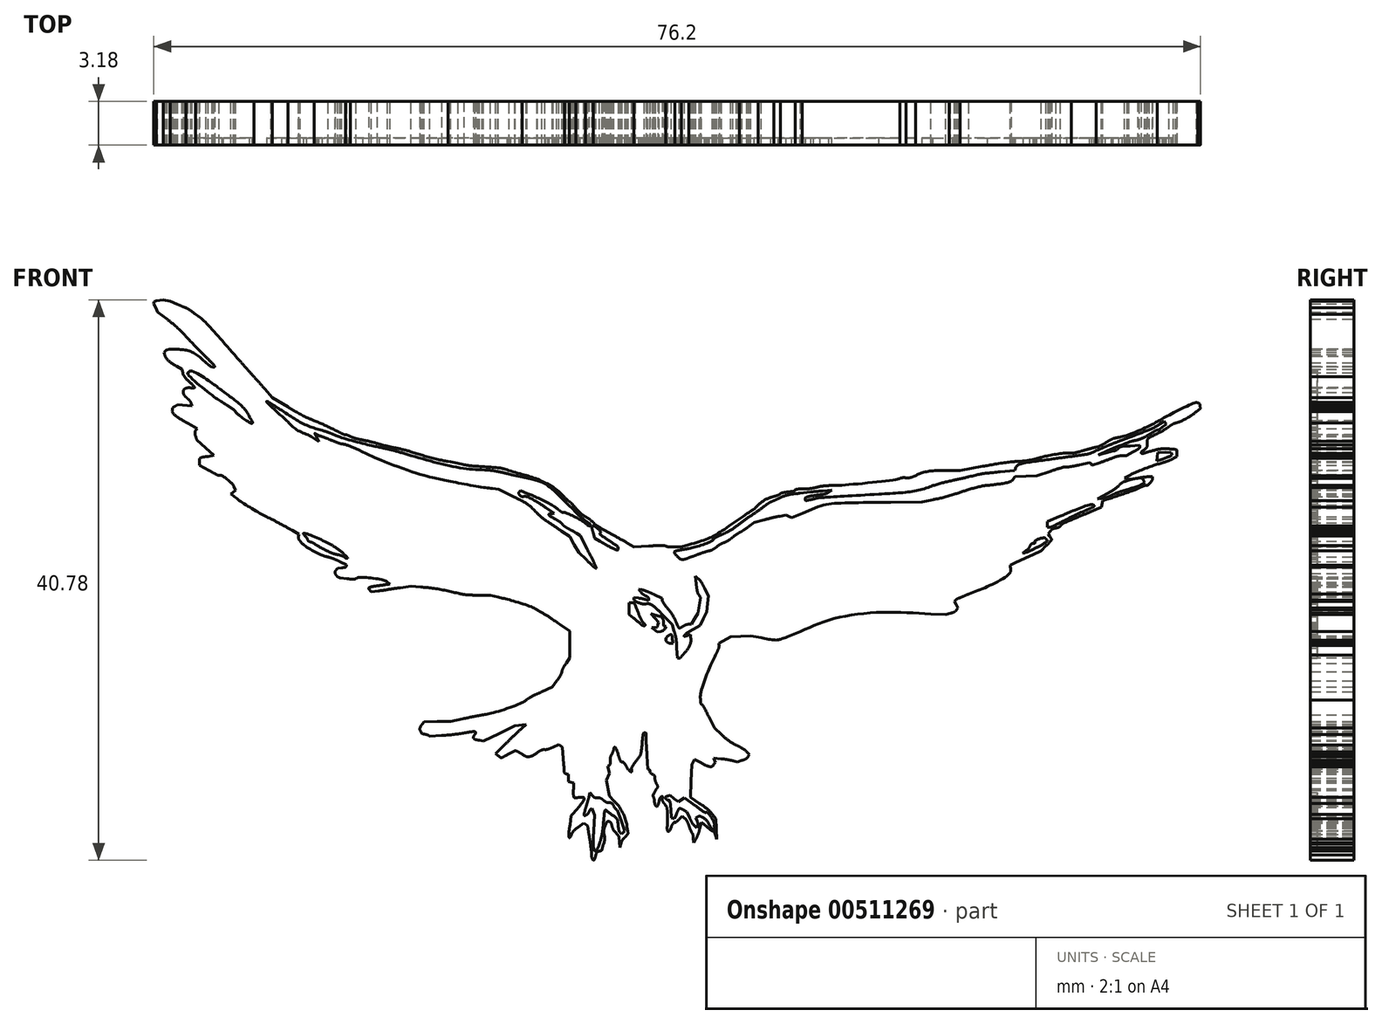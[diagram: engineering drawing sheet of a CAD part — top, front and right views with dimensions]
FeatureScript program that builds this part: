
annotation { "Feature Type Name" : "Feature", "Feature Type Description" : "" }
export const myFeature = defineFeature(function(context is Context, id is Id, definition is map)
    precondition{}
    {
        {
            var Q0;
            Q0=qCreatedBy(makeId("Front.planeOp"),FACE);
            var sketch = newSketch(context, id + "F0", { "sketchPlane" : qUnion([Q0])});
            skFitSpline(sketch, "E0", {"points": [v(-6.24, -23.55) * mm, v(-6.28, -23.27) * mm, v(-6.35, -22.74) * mm, v(-6.4, -22.37) * mm]});
            skFitSpline(sketch, "E1", {"points": [v(-6.51, -21.7) * mm, v(-6.6, -21.64) * mm, v(-6.7, -21.58) * mm, v(-6.8, -21.52) * mm]});
            skLineSegment(sketch, "E2", {"start": v(-6.4, -22.37) * mm, "end": v(-6.51, -21.7) * mm});
            skFitSpline(sketch, "E3", {"points": [v(-7.17, -21.78) * mm, v(-7.37, -21.93) * mm, v(-7.58, -22.14) * mm, v(-7.65, -22.25) * mm]});
            skFitSpline(sketch, "E4", {"points": [v(-7.65, -22.25) * mm, v(-7.83, -22.59) * mm, v(-7.89, -22.36) * mm, v(-7.8, -21.65) * mm]});
            skLineSegment(sketch, "E5", {"start": v(-6.8, -21.52) * mm, "end": v(-7.17, -21.78) * mm});
            skFitSpline(sketch, "E6", {"points": [v(-7.72, -20.99) * mm, v(-7.42, -20.64) * mm, v(-6.77, -19.7) * mm, v(-7.27, -19.67) * mm]});
            skFitSpline(sketch, "E7", {"points": [v(-7.27, -19.67) * mm, v(-7.47, -19.67) * mm, v(-7.54, -19.5) * mm, v(-7.54, -19) * mm]});
            skLineSegment(sketch, "E8", {"start": v(-7.8, -21.65) * mm, "end": v(-7.72, -20.99) * mm});
            skFitSpline(sketch, "E9", {"points": [v(-7.54, -18.6) * mm, v(-7.66, -18.56) * mm, v(-7.78, -18.52) * mm, v(-7.9, -18.49) * mm]});
            skFitSpline(sketch, "E10", {"points": [v(-7.9, -18.49) * mm, v(-7.9, -18.31) * mm, v(-7.9, -18.14) * mm, v(-7.9, -17.97) * mm]});
            skFitSpline(sketch, "E11", {"points": [v(-7.9, -17.97) * mm, v(-8.05, -17.94) * mm, v(-8.18, -17.87) * mm, v(-8.23, -17.75) * mm]});
            skFitSpline(sketch, "E12", {"points": [v(-8.23, -17.75) * mm, v(-8.23, -17.7) * mm, v(-8.25, -17.27) * mm, v(-8.3, -16.82) * mm]});
            skLineSegment(sketch, "E13", {"start": v(-7.54, -19) * mm, "end": v(-7.54, -18.6) * mm});
            skFitSpline(sketch, "E14", {"points": [v(-8.37, -16) * mm, v(-8.44, -15.93) * mm, v(-8.52, -15.86) * mm, v(-8.6, -15.8) * mm]});
            skLineSegment(sketch, "E15", {"start": v(-8.3, -16.82) * mm, "end": v(-8.37, -16) * mm});
            skFitSpline(sketch, "E16", {"points": [v(-9.02, -15.98) * mm, v(-9.26, -16.08) * mm, v(-9.53, -16.16) * mm, v(-9.64, -16.16) * mm]});
            skFitSpline(sketch, "E17", {"points": [v(-9.64, -16.16) * mm, v(-9.75, -16.16) * mm, v(-10, -16.26) * mm, v(-10.2, -16.38) * mm]});
            skFitSpline(sketch, "E18", {"points": [v(-10.2, -16.38) * mm, v(-10.6, -16.64) * mm, v(-10.99, -16.67) * mm, v(-11.32, -16.48) * mm]});
            skFitSpline(sketch, "E19", {"points": [v(-11.32, -16.48) * mm, v(-11.47, -16.4) * mm, v(-11.62, -16.3) * mm, v(-11.77, -16.23) * mm]});
            skLineSegment(sketch, "E20", {"start": v(-8.6, -15.8) * mm, "end": v(-9.02, -15.98) * mm});
            skFitSpline(sketch, "E21", {"points": [v(-12.23, -16.47) * mm, v(-12.75, -16.74) * mm, v(-12.84, -16.75) * mm, v(-13.06, -16.58) * mm]});
            skLineSegment(sketch, "E22", {"start": v(-11.77, -16.23) * mm, "end": v(-12.23, -16.47) * mm});
            skFitSpline(sketch, "E23", {"points": [v(-12.45, -15.7) * mm, v(-12.02, -15.29) * mm, v(-11.52, -14.82) * mm, v(-11.34, -14.65) * mm]});
            skLineSegment(sketch, "E24", {"start": v(-13.06, -16.58) * mm, "end": v(-13.23, -16.46) * mm});
            skLineSegment(sketch, "E25", {"start": v(-13.23, -16.46) * mm, "end": v(-12.45, -15.7) * mm});
            skFitSpline(sketch, "E26", {"points": [v(-11, -14.35) * mm, v(-11.27, -14.38) * mm, v(-11.54, -14.4) * mm, v(-11.81, -14.43) * mm]});
            skLineSegment(sketch, "E27", {"start": v(-11.34, -14.65) * mm, "end": v(-11, -14.35) * mm});
            skFitSpline(sketch, "E28", {"points": [v(-14.4, -15.48) * mm, v(-14.74, -15.4) * mm, v(-14.84, -15.29) * mm, v(-14.72, -15.07) * mm]});
            skFitSpline(sketch, "E29", {"points": [v(-14.72, -15.07) * mm, v(-14.68, -14.99) * mm, v(-14.67, -14.9) * mm, v(-14.7, -14.87) * mm]});
            skFitSpline(sketch, "E30", {"points": [v(-14.7, -14.87) * mm, v(-14.75, -14.85) * mm, v(-15.12, -14.89) * mm, v(-15.54, -14.96) * mm]});
            skFitSpline(sketch, "E31", {"points": [v(-15.54, -14.96) * mm, v(-15.96, -15.03) * mm, v(-16.69, -15.1) * mm, v(-17.16, -15.13) * mm]});
            skLineSegment(sketch, "E32", {"start": v(-11.81, -14.43) * mm, "end": v(-12.96, -14.99) * mm});
            skLineSegment(sketch, "E33", {"start": v(-12.96, -14.99) * mm, "end": v(-14.1, -15.55) * mm});
            skLineSegment(sketch, "E34", {"start": v(-14.1, -15.55) * mm, "end": v(-14.4, -15.48) * mm});
            skFitSpline(sketch, "E35", {"points": [v(-18, -15.19) * mm, v(-18.22, -15.08) * mm, v(-18.58, -14.98) * mm, v(-18.64, -14.86) * mm]});
            skFitSpline(sketch, "E36", {"points": [v(-18.64, -14.86) * mm, v(-18.73, -14.71) * mm, v(-18.66, -14.47) * mm, v(-18.56, -14.32) * mm]});
            skLineSegment(sketch, "E37", {"start": v(-17.16, -15.13) * mm, "end": v(-18, -15.19) * mm});
            skFitSpline(sketch, "E38", {"points": [v(-15.58, -13.92) * mm, v(-15.09, -13.82) * mm, v(-14.46, -13.7) * mm, v(-14.2, -13.64) * mm]});
            skFitSpline(sketch, "E39", {"points": [v(-14.2, -13.64) * mm, v(-13.41, -13.49) * mm, v(-11.3, -12.76) * mm, v(-10.94, -12.52) * mm]});
            skFitSpline(sketch, "E40", {"points": [v(-10.94, -12.52) * mm, v(-10.75, -12.4) * mm, v(-10.26, -12.14) * mm, v(-9.85, -11.95) * mm]});
            skLineSegment(sketch, "E41", {"start": v(-18.56, -14.32) * mm, "end": v(-18.43, -14.14) * mm});
            skLineSegment(sketch, "E42", {"start": v(-18.43, -14.14) * mm, "end": v(-17.46, -14.13) * mm});
            skLineSegment(sketch, "E43", {"start": v(-17.46, -14.13) * mm, "end": v(-16.48, -14.1) * mm});
            skLineSegment(sketch, "E44", {"start": v(-16.48, -14.1) * mm, "end": v(-15.58, -13.92) * mm});
            skFitSpline(sketch, "E45", {"points": [v(-8.77, -11.16) * mm, v(-8.6, -10.92) * mm, v(-8.43, -10.63) * mm, v(-8.4, -10.5) * mm]});
            skFitSpline(sketch, "E46", {"points": [v(-8.4, -10.5) * mm, v(-8.36, -10.38) * mm, v(-8.22, -10.1) * mm, v(-8.07, -9.88) * mm]});
            skLineSegment(sketch, "E47", {"start": v(-9.85, -11.95) * mm, "end": v(-9.09, -11.6) * mm});
            skLineSegment(sketch, "E48", {"start": v(-9.09, -11.6) * mm, "end": v(-8.77, -11.16) * mm});
            skFitSpline(sketch, "E49", {"points": [v(-8.52, -7.07) * mm, v(-9.26, -6.55) * mm, v(-9.66, -6.3) * mm, v(-10.16, -6.02) * mm]});
            skFitSpline(sketch, "E50", {"points": [v(-10.16, -6.02) * mm, v(-10.52, -5.82) * mm, v(-12.11, -5.3) * mm, v(-13.02, -5.08) * mm]});
            skLineSegment(sketch, "E51", {"start": v(-8.07, -9.88) * mm, "end": v(-7.8, -9.48) * mm});
            skLineSegment(sketch, "E52", {"start": v(-7.8, -9.48) * mm, "end": v(-7.82, -8.51) * mm});
            skLineSegment(sketch, "E53", {"start": v(-7.82, -8.51) * mm, "end": v(-7.83, -7.55) * mm});
            skLineSegment(sketch, "E54", {"start": v(-7.83, -7.55) * mm, "end": v(-8.52, -7.07) * mm});
            skFitSpline(sketch, "E55", {"points": [v(-14.5, -4.93) * mm, v(-15, -4.92) * mm, v(-15.65, -4.86) * mm, v(-15.94, -4.8) * mm]});
            skFitSpline(sketch, "E56", {"points": [v(-15.94, -4.8) * mm, v(-16.93, -4.57) * mm, v(-17.95, -4.4) * mm, v(-18.66, -4.34) * mm]});
            skLineSegment(sketch, "E57", {"start": v(-13.02, -5.08) * mm, "end": v(-13.6, -4.94) * mm});
            skLineSegment(sketch, "E58", {"start": v(-13.6, -4.94) * mm, "end": v(-14.5, -4.93) * mm});
            skFitSpline(sketch, "E59", {"points": [v(-20.12, -4.38) * mm, v(-20.54, -4.44) * mm, v(-20.97, -4.5) * mm, v(-21.07, -4.52) * mm]});
            skFitSpline(sketch, "E60", {"points": [v(-21.07, -4.52) * mm, v(-21.17, -4.54) * mm, v(-21.48, -4.58) * mm, v(-21.75, -4.62) * mm]});
            skLineSegment(sketch, "E61", {"start": v(-18.66, -4.34) * mm, "end": v(-19.36, -4.28) * mm});
            skLineSegment(sketch, "E62", {"start": v(-19.36, -4.28) * mm, "end": v(-20.12, -4.38) * mm});
            skFitSpline(sketch, "E63", {"points": [v(-22.25, -4.68) * mm, v(-22.44, -4.4) * mm, v(-21.99, -4.27) * mm, v(-21.86, -4.25) * mm]});
            skFitSpline(sketch, "E64", {"points": [v(-21.86, -4.25) * mm, v(-21.54, -4.2) * mm, v(-21.23, -4.16) * mm, v(-20.9, -4.11) * mm]});
            skLineSegment(sketch, "E65", {"start": v(-21.75, -4.62) * mm, "end": v(-22.25, -4.68) * mm});
            skFitSpline(sketch, "E66", {"points": [v(-21.07, -4) * mm, v(-21.28, -3.86) * mm, v(-23.16, -3.64) * mm, v(-23.38, -3.73) * mm]});
            skFitSpline(sketch, "E67", {"points": [v(-23.38, -3.73) * mm, v(-23.47, -3.76) * mm, v(-23.76, -3.76) * mm, v(-24.03, -3.72) * mm]});
            skLineSegment(sketch, "E68", {"start": v(-20.9, -4.11) * mm, "end": v(-21.07, -4) * mm});
            skFitSpline(sketch, "E69", {"points": [v(-24.52, -3.66) * mm, v(-24.7, -3.6) * mm, v(-24.8, -3.5) * mm, v(-24.89, -3.36) * mm]});
            skFitSpline(sketch, "E70", {"points": [v(-24.89, -3.36) * mm, v(-24.89, -3.2) * mm, v(-24.8, -3.05) * mm, v(-24.7, -2.97) * mm]});
            skLineSegment(sketch, "E71", {"start": v(-24.03, -3.72) * mm, "end": v(-24.52, -3.66) * mm});
            skFitSpline(sketch, "E72", {"points": [v(-24.42, -2.94) * mm, v(-24.23, -2.9) * mm, v(-24.12, -2.88) * mm, v(-24.07, -2.71) * mm]});
            skLineSegment(sketch, "E73", {"start": v(-24.7, -2.97) * mm, "end": v(-24.42, -2.94) * mm});
            skFitSpline(sketch, "E74", {"points": [v(-24.54, -2.5) * mm, v(-24.8, -2.37) * mm, v(-25.2, -2.22) * mm, v(-25.42, -2.15) * mm]});
            skFitSpline(sketch, "E75", {"points": [v(-25.42, -2.15) * mm, v(-25.9, -2) * mm, v(-27.2, -1.26) * mm, v(-27.43, -1) * mm]});
            skFitSpline(sketch, "E76", {"points": [v(-27.43, -1) * mm, v(-27.52, -0.9) * mm, v(-27.58, -0.74) * mm, v(-27.56, -0.65) * mm]});
            skLineSegment(sketch, "E77", {"start": v(-24.07, -2.71) * mm, "end": v(-24.54, -2.5) * mm});
            skFitSpline(sketch, "E78", {"points": [v(-28.02, -0.2) * mm, v(-28.3, -0.05) * mm, v(-28.98, 0.32) * mm, v(-29.55, 0.61) * mm]});
            skFitSpline(sketch, "E79", {"points": [v(-29.55, 0.61) * mm, v(-30.46, 1.08) * mm, v(-31.74, 1.87) * mm, v(-32.3, 2.3) * mm]});
            skLineSegment(sketch, "E80", {"start": v(-27.56, -0.65) * mm, "end": v(-27.52, -0.49) * mm});
            skLineSegment(sketch, "E81", {"start": v(-27.52, -0.49) * mm, "end": v(-28.02, -0.2) * mm});
            skFitSpline(sketch, "E82", {"points": [v(-32.47, 2.43) * mm, v(-32.36, 2.52) * mm, v(-32.24, 2.6) * mm, v(-32.13, 2.7) * mm]});
            skLineSegment(sketch, "E83", {"start": v(-32.3, 2.3) * mm, "end": v(-32.47, 2.43) * mm});
            skFitSpline(sketch, "E84", {"points": [v(-32.25, 2.94) * mm, v(-32.37, 3.15) * mm, v(-33.18, 3.78) * mm, v(-33.35, 3.78) * mm]});
            skFitSpline(sketch, "E85", {"points": [v(-33.35, 3.78) * mm, v(-33.38, 3.78) * mm, v(-33.72, 3.95) * mm, v(-34.09, 4.16) * mm]});
            skLineSegment(sketch, "E86", {"start": v(-32.13, 2.7) * mm, "end": v(-32.25, 2.94) * mm});
            skFitSpline(sketch, "E87", {"points": [v(-34.76, 4.73) * mm, v(-34.76, 5) * mm, v(-34.62, 5.1) * mm, v(-34.14, 5.17) * mm]});
            skLineSegment(sketch, "E88", {"start": v(-34.09, 4.16) * mm, "end": v(-34.76, 4.53) * mm});
            skLineSegment(sketch, "E89", {"start": v(-34.76, 4.53) * mm, "end": v(-34.76, 4.73) * mm});
            skFitSpline(sketch, "E90", {"points": [v(-34.95, 6.37) * mm, v(-35.07, 6.68) * mm, v(-35.09, 7) * mm, v(-34.93, 7.18) * mm]});
            skLineSegment(sketch, "E91", {"start": v(-34.14, 5.17) * mm, "end": v(-33.74, 5.24) * mm});
            skLineSegment(sketch, "E92", {"start": v(-33.74, 5.24) * mm, "end": v(-34.34, 5.8) * mm});
            skLineSegment(sketch, "E93", {"start": v(-34.34, 5.8) * mm, "end": v(-34.95, 6.37) * mm});
            skFitSpline(sketch, "E94", {"points": [v(-35.59, 7.56) * mm, v(-36.27, 7.96) * mm, v(-36.74, 8.38) * mm, v(-36.74, 8.6) * mm]});
            skFitSpline(sketch, "E95", {"points": [v(-36.74, 8.6) * mm, v(-36.74, 8.66) * mm, v(-36.65, 8.76) * mm, v(-36.54, 8.82) * mm]});
            skLineSegment(sketch, "E96", {"start": v(-34.93, 7.18) * mm, "end": v(-35.59, 7.56) * mm});
            skFitSpline(sketch, "E97", {"points": [v(-35.37, 9) * mm, v(-35.39, 9.08) * mm, v(-35.53, 9.26) * mm, v(-35.67, 9.4) * mm]});
            skFitSpline(sketch, "E98", {"points": [v(-35.67, 9.4) * mm, v(-35.81, 9.54) * mm, v(-35.93, 9.72) * mm, v(-35.93, 9.81) * mm]});
            skFitSpline(sketch, "E99", {"points": [v(-35.93, 9.81) * mm, v(-35.93, 10) * mm, v(-35.68, 10.16) * mm, v(-35.4, 10.16) * mm]});
            skFitSpline(sketch, "E100", {"points": [v(-35.4, 10.16) * mm, v(-35.13, 10.16) * mm, v(-35.17, 10.26) * mm, v(-35.57, 10.65) * mm]});
            skFitSpline(sketch, "E101", {"points": [v(-35.57, 10.65) * mm, v(-35.76, 10.84) * mm, v(-35.95, 11.11) * mm, v(-35.98, 11.25) * mm]});
            skLineSegment(sketch, "E102", {"start": v(-36.54, 8.82) * mm, "end": v(-36.35, 8.92) * mm});
            skLineSegment(sketch, "E103", {"start": v(-36.35, 8.92) * mm, "end": v(-35.84, 8.88) * mm});
            skLineSegment(sketch, "E104", {"start": v(-35.84, 8.88) * mm, "end": v(-35.32, 8.83) * mm});
            skLineSegment(sketch, "E105", {"start": v(-35.32, 8.83) * mm, "end": v(-35.37, 9) * mm});
            skFitSpline(sketch, "E106", {"points": [v(-36.41, 11.73) * mm, v(-36.81, 11.96) * mm, v(-37.22, 12.36) * mm, v(-37.3, 12.59) * mm]});
            skLineSegment(sketch, "E107", {"start": v(-35.98, 11.25) * mm, "end": v(-36.03, 11.5) * mm});
            skLineSegment(sketch, "E108", {"start": v(-36.03, 11.5) * mm, "end": v(-36.41, 11.73) * mm});
            skFitSpline(sketch, "E109", {"points": [v(-36.6, 12.95) * mm, v(-35.78, 12.9) * mm, v(-35.02, 12.6) * mm, v(-34.3, 12) * mm]});
            skFitSpline(sketch, "E110", {"points": [v(-34.3, 12) * mm, v(-34.1, 11.82) * mm, v(-33.9, 11.69) * mm, v(-33.86, 11.69) * mm]});
            skFitSpline(sketch, "E111", {"points": [v(-33.86, 11.69) * mm, v(-33.66, 11.69) * mm, v(-33.81, 11.91) * mm, v(-34.34, 12.44) * mm]});
            skFitSpline(sketch, "E112", {"points": [v(-34.34, 12.44) * mm, v(-34.64, 12.74) * mm, v(-35.25, 13.36) * mm, v(-35.67, 13.8) * mm]});
            skFitSpline(sketch, "E113", {"points": [v(-35.67, 13.8) * mm, v(-36.1, 14.26) * mm, v(-36.76, 14.86) * mm, v(-37.13, 15.15) * mm]});
            skLineSegment(sketch, "E114", {"start": v(-37.3, 12.59) * mm, "end": v(-37.35, 12.73) * mm});
            skLineSegment(sketch, "E115", {"start": v(-37.35, 12.73) * mm, "end": v(-37.19, 12.9) * mm});
            skLineSegment(sketch, "E116", {"start": v(-37.19, 12.9) * mm, "end": v(-36.96, 12.97) * mm});
            skLineSegment(sketch, "E117", {"start": v(-36.96, 12.97) * mm, "end": v(-36.6, 12.95) * mm});
            skFitSpline(sketch, "E118", {"points": [v(-36.39, 16.24) * mm, v(-36.11, 16.12) * mm, v(-35.83, 16) * mm, v(-35.75, 15.97) * mm]});
            skFitSpline(sketch, "E119", {"points": [v(-35.75, 15.97) * mm, v(-35.68, 15.95) * mm, v(-35.36, 15.74) * mm, v(-35.06, 15.5) * mm]});
            skFitSpline(sketch, "E120", {"points": [v(-35.06, 15.5) * mm, v(-34.53, 15.1) * mm, v(-33.65, 14.19) * mm, v(-31.84, 12.14) * mm]});
            skFitSpline(sketch, "E121", {"points": [v(-31.84, 12.14) * mm, v(-31.4, 11.63) * mm, v(-30.93, 11.1) * mm, v(-30.81, 10.97) * mm]});
            skFitSpline(sketch, "E122", {"points": [v(-30.81, 10.97) * mm, v(-30.69, 10.84) * mm, v(-30.33, 10.44) * mm, v(-30.02, 10.09) * mm]});
            skLineSegment(sketch, "E123", {"start": v(-37.13, 15.15) * mm, "end": v(-37.81, 15.67) * mm});
            skLineSegment(sketch, "E124", {"start": v(-37.81, 15.67) * mm, "end": v(-37.96, 15.98) * mm});
            skLineSegment(sketch, "E125", {"start": v(-37.96, 15.98) * mm, "end": v(-38.1, 16.28) * mm});
            skLineSegment(sketch, "E126", {"start": v(-38.1, 16.28) * mm, "end": v(-38.07, 16.42) * mm});
            skLineSegment(sketch, "E127", {"start": v(-38.07, 16.42) * mm, "end": v(-37.92, 16.5) * mm});
            skLineSegment(sketch, "E128", {"start": v(-37.92, 16.5) * mm, "end": v(-37.42, 16.57) * mm});
            skLineSegment(sketch, "E129", {"start": v(-37.42, 16.57) * mm, "end": v(-36.89, 16.46) * mm});
            skLineSegment(sketch, "E130", {"start": v(-36.89, 16.46) * mm, "end": v(-36.39, 16.24) * mm});
            skFitSpline(sketch, "E131", {"points": [v(-28.33, 8.77) * mm, v(-27.72, 8.4) * mm, v(-26.86, 7.95) * mm, v(-26.43, 7.77) * mm]});
            skFitSpline(sketch, "E132", {"points": [v(-26.43, 7.77) * mm, v(-26, 7.6) * mm, v(-25.33, 7.3) * mm, v(-24.94, 7.1) * mm]});
            skFitSpline(sketch, "E133", {"points": [v(-24.94, 7.1) * mm, v(-24.54, 6.9) * mm, v(-24.18, 6.74) * mm, v(-24.14, 6.74) * mm]});
            skFitSpline(sketch, "E134", {"points": [v(-24.14, 6.74) * mm, v(-24.1, 6.74) * mm, v(-23.93, 6.69) * mm, v(-23.77, 6.62) * mm]});
            skFitSpline(sketch, "E135", {"points": [v(-23.77, 6.62) * mm, v(-23.62, 6.55) * mm, v(-23.2, 6.43) * mm, v(-22.86, 6.36) * mm]});
            skFitSpline(sketch, "E136", {"points": [v(-22.86, 6.36) * mm, v(-22.51, 6.29) * mm, v(-22, 6.16) * mm, v(-21.74, 6.08) * mm]});
            skFitSpline(sketch, "E137", {"points": [v(-21.74, 6.08) * mm, v(-21.47, 6) * mm, v(-20.94, 5.88) * mm, v(-20.57, 5.8) * mm]});
            skFitSpline(sketch, "E138", {"points": [v(-20.57, 5.8) * mm, v(-20.2, 5.72) * mm, v(-19.63, 5.58) * mm, v(-19.31, 5.48) * mm]});
            skFitSpline(sketch, "E139", {"points": [v(-19.31, 5.48) * mm, v(-18.41, 5.21) * mm, v(-17.35, 4.94) * mm, v(-16.66, 4.8) * mm]});
            skFitSpline(sketch, "E140", {"points": [v(-16.66, 4.8) * mm, v(-15.32, 4.53) * mm, v(-15.1, 4.5) * mm, v(-14.04, 4.41) * mm]});
            skFitSpline(sketch, "E141", {"points": [v(-14.04, 4.41) * mm, v(-12.89, 4.33) * mm, v(-12.7, 4.29) * mm, v(-11.27, 3.85) * mm]});
            skFitSpline(sketch, "E142", {"points": [v(-11.27, 3.85) * mm, v(-10.21, 3.53) * mm, v(-8.79, 2.76) * mm, v(-8.2, 2.2) * mm]});
            skFitSpline(sketch, "E143", {"points": [v(-8.2, 2.2) * mm, v(-8.1, 2.1) * mm, v(-7.94, 1.97) * mm, v(-7.85, 1.89) * mm]});
            skFitSpline(sketch, "E144", {"points": [v(-7.85, 1.89) * mm, v(-7.76, 1.81) * mm, v(-7.54, 1.59) * mm, v(-7.36, 1.39) * mm]});
            skFitSpline(sketch, "E145", {"points": [v(-7.36, 1.39) * mm, v(-7.2, 1.19) * mm, v(-6.88, 0.92) * mm, v(-6.68, 0.79) * mm]});
            skFitSpline(sketch, "E146", {"points": [v(-6.68, 0.79) * mm, v(-6.47, 0.66) * mm, v(-6.2, 0.46) * mm, v(-6.1, 0.34) * mm]});
            skFitSpline(sketch, "E147", {"points": [v(-6.1, 0.34) * mm, v(-5.97, 0.23) * mm, v(-5.46, -0.1) * mm, v(-4.94, -0.4) * mm]});
            skFitSpline(sketch, "E148", {"points": [v(-4.94, -0.4) * mm, v(-4.42, -0.68) * mm, v(-3.8, -1.03) * mm, v(-3.58, -1.16) * mm]});
            skLineSegment(sketch, "E149", {"start": v(-30.02, 10.09) * mm, "end": v(-29.46, 9.45) * mm});
            skLineSegment(sketch, "E150", {"start": v(-29.46, 9.45) * mm, "end": v(-28.33, 8.77) * mm});
            skFitSpline(sketch, "E151", {"points": [v(-2.07, -1.35) * mm, v(-1.47, -1.32) * mm, v(-0.91, -1.32) * mm, v(-0.83, -1.36) * mm]});
            skFitSpline(sketch, "E152", {"points": [v(-0.83, -1.36) * mm, v(-0.74, -1.39) * mm, v(-0.45, -1.42) * mm, v(-0.18, -1.42) * mm]});
            skLineSegment(sketch, "E153", {"start": v(-3.58, -1.16) * mm, "end": v(-3.16, -1.41) * mm});
            skLineSegment(sketch, "E154", {"start": v(-3.16, -1.41) * mm, "end": v(-2.07, -1.35) * mm});
            skFitSpline(sketch, "E155", {"points": [v(0.85, -1.26) * mm, v(2.23, -0.82) * mm, v(2.98, -0.44) * mm, v(4.53, 0.61) * mm]});
            skFitSpline(sketch, "E156", {"points": [v(4.53, 0.61) * mm, v(5.51, 1.29) * mm, v(5.64, 1.38) * mm, v(5.91, 1.63) * mm]});
            skFitSpline(sketch, "E157", {"points": [v(5.91, 1.63) * mm, v(6.15, 1.85) * mm, v(6.66, 2.13) * mm, v(7.05, 2.25) * mm]});
            skFitSpline(sketch, "E158", {"points": [v(7.05, 2.25) * mm, v(7.25, 2.32) * mm, v(7.46, 2.4) * mm, v(7.52, 2.45) * mm]});
            skFitSpline(sketch, "E159", {"points": [v(7.52, 2.45) * mm, v(7.57, 2.5) * mm, v(7.83, 2.55) * mm, v(8.08, 2.58) * mm]});
            skFitSpline(sketch, "E160", {"points": [v(8.08, 2.58) * mm, v(8.33, 2.61) * mm, v(8.56, 2.67) * mm, v(8.59, 2.71) * mm]});
            skFitSpline(sketch, "E161", {"points": [v(8.59, 2.71) * mm, v(8.61, 2.76) * mm, v(8.85, 2.8) * mm, v(9.1, 2.8) * mm]});
            skFitSpline(sketch, "E162", {"points": [v(9.1, 2.8) * mm, v(9.36, 2.8) * mm, v(9.81, 2.85) * mm, v(10.1, 2.91) * mm]});
            skFitSpline(sketch, "E163", {"points": [v(10.1, 2.91) * mm, v(10.4, 2.98) * mm, v(10.9, 3.04) * mm, v(11.23, 3.05) * mm]});
            skFitSpline(sketch, "E164", {"points": [v(11.23, 3.05) * mm, v(11.98, 3.08) * mm, v(15.98, 3.5) * mm, v(16.22, 3.57) * mm]});
            skFitSpline(sketch, "E165", {"points": [v(16.22, 3.57) * mm, v(16.31, 3.6) * mm, v(16.52, 3.62) * mm, v(16.67, 3.61) * mm]});
            skFitSpline(sketch, "E166", {"points": [v(16.67, 3.61) * mm, v(16.82, 3.6) * mm, v(17.12, 3.67) * mm, v(17.35, 3.77) * mm]});
            skFitSpline(sketch, "E167", {"points": [v(17.35, 3.77) * mm, v(17.88, 4) * mm, v(18.84, 4.14) * mm, v(19.81, 4.14) * mm]});
            skLineSegment(sketch, "E168", {"start": v(-0.18, -1.42) * mm, "end": v(0.32, -1.43) * mm});
            skLineSegment(sketch, "E169", {"start": v(0.32, -1.43) * mm, "end": v(0.85, -1.26) * mm});
            skFitSpline(sketch, "E170", {"points": [v(22.26, 4.44) * mm, v(23.19, 4.61) * mm, v(24.3, 4.77) * mm, v(24.75, 4.8) * mm]});
            skFitSpline(sketch, "E171", {"points": [v(24.75, 4.8) * mm, v(25.2, 4.83) * mm, v(25.88, 4.94) * mm, v(26.27, 5.04) * mm]});
            skFitSpline(sketch, "E172", {"points": [v(26.27, 5.04) * mm, v(26.94, 5.2) * mm, v(28.3, 5.42) * mm, v(28.7, 5.4) * mm]});
            skFitSpline(sketch, "E173", {"points": [v(28.7, 5.4) * mm, v(28.8, 5.4) * mm, v(29.18, 5.49) * mm, v(29.55, 5.59) * mm]});
            skFitSpline(sketch, "E174", {"points": [v(29.55, 5.59) * mm, v(29.93, 5.69) * mm, v(30.35, 5.8) * mm, v(30.5, 5.84) * mm]});
            skFitSpline(sketch, "E175", {"points": [v(30.5, 5.84) * mm, v(30.65, 5.88) * mm, v(30.97, 6.03) * mm, v(31.22, 6.18) * mm]});
            skFitSpline(sketch, "E176", {"points": [v(31.22, 6.18) * mm, v(31.46, 6.33) * mm, v(31.79, 6.48) * mm, v(31.94, 6.51) * mm]});
            skFitSpline(sketch, "E177", {"points": [v(31.94, 6.51) * mm, v(32.53, 6.65) * mm, v(34.27, 7.33) * mm, v(34.95, 7.7) * mm]});
            skFitSpline(sketch, "E178", {"points": [v(34.95, 7.7) * mm, v(35.91, 8.23) * mm, v(37.78, 9.08) * mm, v(37.9, 9.06) * mm]});
            skFitSpline(sketch, "E179", {"points": [v(37.9, 9.06) * mm, v(37.98, 9.05) * mm, v(38.06, 8.95) * mm, v(38.07, 8.84) * mm]});
            skLineSegment(sketch, "E180", {"start": v(19.81, 4.14) * mm, "end": v(20.59, 4.14) * mm});
            skLineSegment(sketch, "E181", {"start": v(20.59, 4.14) * mm, "end": v(22.26, 4.44) * mm});
            skFitSpline(sketch, "E182", {"points": [v(37.8, 8.42) * mm, v(37.45, 8.15) * mm, v(36.6, 7.7) * mm, v(36.3, 7.6) * mm]});
            skFitSpline(sketch, "E183", {"points": [v(36.3, 7.6) * mm, v(36.17, 7.56) * mm, v(35.94, 7.44) * mm, v(35.79, 7.32) * mm]});
            skFitSpline(sketch, "E184", {"points": [v(35.79, 7.32) * mm, v(35.64, 7.2) * mm, v(35.27, 7) * mm, v(34.97, 6.84) * mm]});
            skFitSpline(sketch, "E185", {"points": [v(34.97, 6.84) * mm, v(34.45, 6.58) * mm, v(34.25, 6.42) * mm, v(34.23, 6.27) * mm]});
            skFitSpline(sketch, "E186", {"points": [v(34.23, 6.27) * mm, v(34.23, 6.24) * mm, v(34.23, 6.13) * mm, v(34.23, 6.03) * mm]});
            skFitSpline(sketch, "E187", {"points": [v(34.23, 6.03) * mm, v(34.23, 5.93) * mm, v(34.14, 5.77) * mm, v(34.03, 5.67) * mm]});
            skFitSpline(sketch, "E188", {"points": [v(34.03, 5.67) * mm, v(33.78, 5.44) * mm, v(33.84, 5.38) * mm, v(34.23, 5.48) * mm]});
            skFitSpline(sketch, "E189", {"points": [v(34.23, 5.48) * mm, v(34.98, 5.67) * mm, v(35.47, 5.75) * mm, v(35.82, 5.71) * mm]});
            skFitSpline(sketch, "E190", {"points": [v(35.82, 5.71) * mm, v(36.3, 5.67) * mm, v(36.38, 5.62) * mm, v(36.38, 5.37) * mm]});
            skLineSegment(sketch, "E191", {"start": v(38.07, 8.84) * mm, "end": v(38.1, 8.65) * mm});
            skLineSegment(sketch, "E192", {"start": v(38.1, 8.65) * mm, "end": v(37.8, 8.42) * mm});
            skFitSpline(sketch, "E193", {"points": [v(36.14, 5.02) * mm, v(36, 4.95) * mm, v(35.6, 4.8) * mm, v(35.26, 4.68) * mm]});
            skFitSpline(sketch, "E194", {"points": [v(35.26, 4.68) * mm, v(34.53, 4.46) * mm, v(33.35, 4) * mm, v(32.9, 3.77) * mm]});
            skLineSegment(sketch, "E195", {"start": v(36.38, 5.37) * mm, "end": v(36.38, 5.17) * mm});
            skLineSegment(sketch, "E196", {"start": v(36.38, 5.17) * mm, "end": v(36.14, 5.02) * mm});
            skFitSpline(sketch, "E197", {"points": [v(32.75, 3.54) * mm, v(32.84, 3.5) * mm, v(33.19, 3.53) * mm, v(33.53, 3.58) * mm]});
            skFitSpline(sketch, "E198", {"points": [v(33.53, 3.58) * mm, v(33.86, 3.64) * mm, v(34.24, 3.7) * mm, v(34.36, 3.7) * mm]});
            skLineSegment(sketch, "E199", {"start": v(32.9, 3.77) * mm, "end": v(32.58, 3.6) * mm});
            skLineSegment(sketch, "E200", {"start": v(32.58, 3.6) * mm, "end": v(32.75, 3.54) * mm});
            skFitSpline(sketch, "E201", {"points": [v(34.59, 3.57) * mm, v(34.59, 3.45) * mm, v(34.22, 3.06) * mm, v(34.1, 3.06) * mm]});
            skFitSpline(sketch, "E202", {"points": [v(34.1, 3.06) * mm, v(34.07, 3.06) * mm, v(33.87, 2.99) * mm, v(33.66, 2.9) * mm]});
            skFitSpline(sketch, "E203", {"points": [v(33.66, 2.9) * mm, v(33.34, 2.75) * mm, v(32.4, 2.42) * mm, v(31.28, 2.04) * mm]});
            skLineSegment(sketch, "E204", {"start": v(34.36, 3.7) * mm, "end": v(34.59, 3.7) * mm});
            skLineSegment(sketch, "E205", {"start": v(34.59, 3.7) * mm, "end": v(34.59, 3.57) * mm});
            skFitSpline(sketch, "E206", {"points": [v(30.51, 1.32) * mm, v(30.3, 1.23) * mm, v(29.9, 1.05) * mm, v(29.6, 0.93) * mm]});
            skFitSpline(sketch, "E207", {"points": [v(29.6, 0.93) * mm, v(28.71, 0.56) * mm, v(27.96, 0.2) * mm, v(27.9, 0.1) * mm]});
            skFitSpline(sketch, "E208", {"points": [v(27.9, 0.1) * mm, v(27.87, 0.06) * mm, v(27.73, 0) * mm, v(27.59, -0.04) * mm]});
            skFitSpline(sketch, "E209", {"points": [v(27.59, -0.04) * mm, v(27.45, -0.07) * mm, v(27.26, -0.17) * mm, v(27.17, -0.27) * mm]});
            skLineSegment(sketch, "E210", {"start": v(31.28, 2.04) * mm, "end": v(30.98, 1.94) * mm});
            skLineSegment(sketch, "E211", {"start": v(30.98, 1.94) * mm, "end": v(30.94, 1.71) * mm});
            skLineSegment(sketch, "E212", {"start": v(30.94, 1.71) * mm, "end": v(30.89, 1.49) * mm});
            skLineSegment(sketch, "E213", {"start": v(30.89, 1.49) * mm, "end": v(30.51, 1.32) * mm});
            skFitSpline(sketch, "E214", {"points": [v(27.11, -0.63) * mm, v(27.27, -0.88) * mm, v(27.26, -0.92) * mm, v(26.86, -1.33) * mm]});
            skLineSegment(sketch, "E215", {"start": v(27.17, -0.27) * mm, "end": v(27, -0.45) * mm});
            skLineSegment(sketch, "E216", {"start": v(27, -0.45) * mm, "end": v(27.11, -0.63) * mm});
            skFitSpline(sketch, "E217", {"points": [v(25.9, -1.98) * mm, v(25.56, -2.13) * mm, v(25.06, -2.36) * mm, v(24.77, -2.5) * mm]});
            skLineSegment(sketch, "E218", {"start": v(26.86, -1.33) * mm, "end": v(26.5, -1.7) * mm});
            skLineSegment(sketch, "E219", {"start": v(26.5, -1.7) * mm, "end": v(25.9, -1.98) * mm});
            skFitSpline(sketch, "E220", {"points": [v(24.26, -2.88) * mm, v(24.26, -3.27) * mm, v(22.83, -4.2) * mm, v(21.22, -4.85) * mm]});
            skFitSpline(sketch, "E221", {"points": [v(21.22, -4.85) * mm, v(20.75, -5.04) * mm, v(20.32, -5.24) * mm, v(20.27, -5.3) * mm]});
            skLineSegment(sketch, "E222", {"start": v(24.77, -2.5) * mm, "end": v(24.26, -2.73) * mm});
            skLineSegment(sketch, "E223", {"start": v(24.26, -2.73) * mm, "end": v(24.26, -2.88) * mm});
            skFitSpline(sketch, "E224", {"points": [v(20.33, -6) * mm, v(20.28, -6.08) * mm, v(20.08, -6.2) * mm, v(19.89, -6.25) * mm]});
            skLineSegment(sketch, "E225", {"start": v(20.27, -5.3) * mm, "end": v(20.18, -5.38) * mm});
            skLineSegment(sketch, "E226", {"start": v(20.18, -5.38) * mm, "end": v(20.3, -5.61) * mm});
            skLineSegment(sketch, "E227", {"start": v(20.3, -5.61) * mm, "end": v(20.43, -5.84) * mm});
            skLineSegment(sketch, "E228", {"start": v(20.43, -5.84) * mm, "end": v(20.33, -6) * mm});
            skFitSpline(sketch, "E229", {"points": [v(18.46, -6.3) * mm, v(14.95, -6.17) * mm, v(11.37, -6.65) * mm, v(8.98, -7.58) * mm]});
            skFitSpline(sketch, "E230", {"points": [v(8.98, -7.58) * mm, v(7.6, -8.12) * mm, v(7.1, -8.2) * mm, v(6.11, -8.02) * mm]});
            skLineSegment(sketch, "E231", {"start": v(19.89, -6.25) * mm, "end": v(19.54, -6.35) * mm});
            skLineSegment(sketch, "E232", {"start": v(19.54, -6.35) * mm, "end": v(18.46, -6.3) * mm});
            skFitSpline(sketch, "E233", {"points": [v(3.06, -8.59) * mm, v(3.06, -8.67) * mm, v(2.94, -8.98) * mm, v(2.8, -9.28) * mm]});
            skFitSpline(sketch, "E234", {"points": [v(2.8, -9.28) * mm, v(2.3, -10.34) * mm, v(1.7, -12.13) * mm, v(1.7, -12.54) * mm]});
            skFitSpline(sketch, "E235", {"points": [v(1.7, -12.54) * mm, v(1.7, -12.7) * mm, v(1.75, -12.85) * mm, v(1.8, -12.89) * mm]});
            skFitSpline(sketch, "E236", {"points": [v(1.8, -12.89) * mm, v(1.85, -12.92) * mm, v(2.08, -13.31) * mm, v(2.3, -13.77) * mm]});
            skLineSegment(sketch, "E237", {"start": v(6.11, -8.02) * mm, "end": v(5.35, -7.88) * mm});
            skLineSegment(sketch, "E238", {"start": v(5.35, -7.88) * mm, "end": v(4.62, -7.92) * mm});
            skLineSegment(sketch, "E239", {"start": v(4.62, -7.92) * mm, "end": v(3.9, -7.95) * mm});
            skLineSegment(sketch, "E240", {"start": v(3.9, -7.95) * mm, "end": v(3.47, -8.2) * mm});
            skLineSegment(sketch, "E241", {"start": v(3.47, -8.2) * mm, "end": v(3.06, -8.44) * mm});
            skLineSegment(sketch, "E242", {"start": v(3.06, -8.44) * mm, "end": v(3.06, -8.59) * mm});
            skFitSpline(sketch, "E243", {"points": [v(3.22, -15.06) * mm, v(3.5, -15.32) * mm, v(4, -15.67) * mm, v(4.32, -15.84) * mm]});
            skFitSpline(sketch, "E244", {"points": [v(4.32, -15.84) * mm, v(4.64, -16.01) * mm, v(4.98, -16.24) * mm, v(5.08, -16.34) * mm]});
            skLineSegment(sketch, "E245", {"start": v(2.3, -13.77) * mm, "end": v(2.72, -14.6) * mm});
            skLineSegment(sketch, "E246", {"start": v(2.72, -14.6) * mm, "end": v(3.22, -15.06) * mm});
            skFitSpline(sketch, "E247", {"points": [v(5.15, -16.68) * mm, v(5.1, -16.77) * mm, v(4.9, -16.89) * mm, v(4.72, -16.95) * mm]});
            skLineSegment(sketch, "E248", {"start": v(5.08, -16.34) * mm, "end": v(5.25, -16.53) * mm});
            skLineSegment(sketch, "E249", {"start": v(5.25, -16.53) * mm, "end": v(5.15, -16.68) * mm});
            skFitSpline(sketch, "E250", {"points": [v(4.06, -16.98) * mm, v(3.88, -16.93) * mm, v(3.5, -16.86) * mm, v(3.2, -16.83) * mm]});
            skLineSegment(sketch, "E251", {"start": v(4.72, -16.95) * mm, "end": v(4.38, -17.06) * mm});
            skLineSegment(sketch, "E252", {"start": v(4.38, -17.06) * mm, "end": v(4.06, -16.98) * mm});
            skFitSpline(sketch, "E253", {"points": [v(2.69, -17.2) * mm, v(2.53, -17.4) * mm, v(2.2, -17.36) * mm, v(1.7, -17.1) * mm]});
            skLineSegment(sketch, "E254", {"start": v(3.2, -16.83) * mm, "end": v(2.67, -16.77) * mm});
            skLineSegment(sketch, "E255", {"start": v(2.67, -16.77) * mm, "end": v(2.73, -16.93) * mm});
            skLineSegment(sketch, "E256", {"start": v(2.73, -16.93) * mm, "end": v(2.79, -17.08) * mm});
            skLineSegment(sketch, "E257", {"start": v(2.79, -17.08) * mm, "end": v(2.69, -17.2) * mm});
            skFitSpline(sketch, "E258", {"points": [v(1.62, -20.08) * mm, v(1.98, -20.32) * mm, v(2.4, -20.67) * mm, v(2.56, -20.86) * mm]});
            skLineSegment(sketch, "E259", {"start": v(1.7, -17.1) * mm, "end": v(1.27, -16.88) * mm});
            skLineSegment(sketch, "E260", {"start": v(1.27, -16.88) * mm, "end": v(1.16, -17.07) * mm});
            skLineSegment(sketch, "E261", {"start": v(1.16, -17.07) * mm, "end": v(1.06, -17.26) * mm});
            skLineSegment(sketch, "E262", {"start": v(1.06, -17.26) * mm, "end": v(1.01, -18.45) * mm});
            skLineSegment(sketch, "E263", {"start": v(1.01, -18.45) * mm, "end": v(0.96, -19.64) * mm});
            skLineSegment(sketch, "E264", {"start": v(0.96, -19.64) * mm, "end": v(1.62, -20.08) * mm});
            skFitSpline(sketch, "E265", {"points": [v(2.78, -22.38) * mm, v(2.73, -22.22) * mm, v(2.66, -22.1) * mm, v(2.61, -22.1) * mm]});
            skFitSpline(sketch, "E266", {"points": [v(2.61, -22.1) * mm, v(2.57, -22.1) * mm, v(2.36, -21.95) * mm, v(2.15, -21.77) * mm]});
            skLineSegment(sketch, "E267", {"start": v(2.56, -20.86) * mm, "end": v(2.83, -21.2) * mm});
            skLineSegment(sketch, "E268", {"start": v(2.83, -21.2) * mm, "end": v(2.85, -21.94) * mm});
            skLineSegment(sketch, "E269", {"start": v(2.85, -21.94) * mm, "end": v(2.87, -22.68) * mm});
            skLineSegment(sketch, "E270", {"start": v(2.87, -22.68) * mm, "end": v(2.78, -22.38) * mm});
            skFitSpline(sketch, "E271", {"points": [v(1.65, -21.9) * mm, v(1.58, -22.16) * mm, v(1.46, -22.5) * mm, v(1.37, -22.65) * mm]});
            skLineSegment(sketch, "E272", {"start": v(2.15, -21.77) * mm, "end": v(1.77, -21.45) * mm});
            skLineSegment(sketch, "E273", {"start": v(1.77, -21.45) * mm, "end": v(1.65, -21.9) * mm});
            skFitSpline(sketch, "E274", {"points": [v(1.18, -22.63) * mm, v(1.17, -22.46) * mm, v(1.12, -22.28) * mm, v(1.09, -22.23) * mm]});
            skFitSpline(sketch, "E275", {"points": [v(1.09, -22.23) * mm, v(1.05, -22.18) * mm, v(0.95, -21.95) * mm, v(0.87, -21.72) * mm]});
            skFitSpline(sketch, "E276", {"points": [v(0.87, -21.72) * mm, v(0.78, -21.5) * mm, v(0.64, -21.24) * mm, v(0.55, -21.15) * mm]});
            skLineSegment(sketch, "E277", {"start": v(1.37, -22.65) * mm, "end": v(1.21, -22.94) * mm});
            skLineSegment(sketch, "E278", {"start": v(1.21, -22.94) * mm, "end": v(1.18, -22.63) * mm});
            skFitSpline(sketch, "E279", {"points": [v(0.15, -21.23) * mm, v(0.02, -21.36) * mm, v(-0.12, -21.46) * mm, v(-0.17, -21.46) * mm]});
            skFitSpline(sketch, "E280", {"points": [v(-0.17, -21.46) * mm, v(-0.22, -21.46) * mm, v(-0.33, -21.58) * mm, v(-0.4, -21.73) * mm]});
            skFitSpline(sketch, "E281", {"points": [v(-0.4, -21.73) * mm, v(-0.6, -22.13) * mm, v(-0.7, -22.06) * mm, v(-0.7, -21.53) * mm]});
            skFitSpline(sketch, "E282", {"points": [v(-0.7, -21.53) * mm, v(-0.7, -21.27) * mm, v(-0.7, -20.9) * mm, v(-0.7, -20.71) * mm]});
            skLineSegment(sketch, "E283", {"start": v(0.55, -21.15) * mm, "end": v(0.38, -21) * mm});
            skLineSegment(sketch, "E284", {"start": v(0.38, -21) * mm, "end": v(0.15, -21.23) * mm});
            skFitSpline(sketch, "E285", {"points": [v(-0.9, -20.14) * mm, v(-1, -20.01) * mm, v(-1.08, -19.86) * mm, v(-1.08, -19.79) * mm]});
            skFitSpline(sketch, "E286", {"points": [v(-1.08, -19.79) * mm, v(-1.08, -19.57) * mm, v(-1.21, -19.66) * mm, v(-1.32, -19.94) * mm]});
            skFitSpline(sketch, "E287", {"points": [v(-1.32, -19.94) * mm, v(-1.45, -20.29) * mm, v(-1.58, -20.22) * mm, v(-1.66, -19.76) * mm]});
            skFitSpline(sketch, "E288", {"points": [v(-1.66, -19.76) * mm, v(-1.75, -19.49) * mm, v(-1.7, -19.36) * mm, v(-1.57, -19.12) * mm]});
            skFitSpline(sketch, "E289", {"points": [v(-1.57, -19.12) * mm, v(-1.42, -18.9) * mm, v(-1.42, -18.84) * mm, v(-1.52, -18.62) * mm]});
            skFitSpline(sketch, "E290", {"points": [v(-1.52, -18.62) * mm, v(-1.57, -18.5) * mm, v(-1.62, -18.32) * mm, v(-1.62, -18.23) * mm]});
            skFitSpline(sketch, "E291", {"points": [v(-1.62, -18.23) * mm, v(-1.62, -18.13) * mm, v(-1.7, -18.01) * mm, v(-1.8, -17.96) * mm]});
            skFitSpline(sketch, "E292", {"points": [v(-1.8, -17.96) * mm, v(-1.9, -17.9) * mm, v(-1.97, -17.8) * mm, v(-1.97, -17.73) * mm]});
            skFitSpline(sketch, "E293", {"points": [v(-1.97, -17.73) * mm, v(-2, -17.61) * mm, v(-2.03, -17.6) * mm, v(-2.14, -17.6) * mm]});
            skLineSegment(sketch, "E294", {"start": v(-0.7, -20.71) * mm, "end": v(-0.72, -20.36) * mm});
            skLineSegment(sketch, "E295", {"start": v(-0.72, -20.36) * mm, "end": v(-0.9, -20.14) * mm});
            skFitSpline(sketch, "E296", {"points": [v(-2.2, -16.59) * mm, v(-2.27, -15.07) * mm, v(-2.28, -14.95) * mm, v(-2.38, -14.95) * mm]});
            skFitSpline(sketch, "E297", {"points": [v(-2.38, -14.95) * mm, v(-2.43, -14.95) * mm, v(-2.5, -15.17) * mm, v(-2.52, -15.44) * mm]});
            skFitSpline(sketch, "E298", {"points": [v(-2.52, -15.44) * mm, v(-2.62, -16.34) * mm, v(-2.7, -16.58) * mm, v(-3, -17.02) * mm]});
            skFitSpline(sketch, "E299", {"points": [v(-3, -17.02) * mm, v(-3.18, -17.27) * mm, v(-3.32, -17.51) * mm, v(-3.32, -17.58) * mm]});
            skFitSpline(sketch, "E300", {"points": [v(-3.32, -17.58) * mm, v(-3.32, -17.78) * mm, v(-3.5, -17.7) * mm, v(-3.7, -17.38) * mm]});
            skFitSpline(sketch, "E301", {"points": [v(-3.7, -17.38) * mm, v(-3.81, -17.2) * mm, v(-3.95, -17.06) * mm, v(-4.01, -17.06) * mm]});
            skFitSpline(sketch, "E302", {"points": [v(-4.01, -17.06) * mm, v(-4.07, -17.06) * mm, v(-4.18, -16.86) * mm, v(-4.26, -16.61) * mm]});
            skFitSpline(sketch, "E303", {"points": [v(-4.26, -16.61) * mm, v(-4.43, -16.11) * mm, v(-4.56, -15.98) * mm, v(-4.63, -16.22) * mm]});
            skFitSpline(sketch, "E304", {"points": [v(-4.63, -16.22) * mm, v(-4.73, -16.47) * mm, v(-4.85, -16.71) * mm, v(-4.85, -16.96) * mm]});
            skFitSpline(sketch, "E305", {"points": [v(-4.85, -16.96) * mm, v(-4.86, -17.15) * mm, v(-4.9, -17.26) * mm, v(-5.04, -17.35) * mm]});
            skFitSpline(sketch, "E306", {"points": [v(-5.04, -17.35) * mm, v(-5, -17.53) * mm, v(-4.96, -17.7) * mm, v(-4.92, -17.88) * mm]});
            skFitSpline(sketch, "E307", {"points": [v(-4.92, -17.88) * mm, v(-5, -18.06) * mm, v(-5.07, -18.23) * mm, v(-5.14, -18.4) * mm]});
            skFitSpline(sketch, "E308", {"points": [v(-5.14, -18.4) * mm, v(-5.07, -18.79) * mm, v(-5, -19.17) * mm, v(-4.92, -19.56) * mm]});
            skLineSegment(sketch, "E309", {"start": v(-2.14, -17.6) * mm, "end": v(-2.2, -16.59) * mm});
            skFitSpline(sketch, "E310", {"points": [v(-4.6, -19.9) * mm, v(-4.24, -20.28) * mm, v(-3.73, -21.33) * mm, v(-3.64, -21.9) * mm]});
            skLineSegment(sketch, "E311", {"start": v(-4.92, -19.56) * mm, "end": v(-4.6, -19.9) * mm});
            skFitSpline(sketch, "E312", {"points": [v(-3.8, -22.53) * mm, v(-3.92, -22.66) * mm, v(-4.05, -22.89) * mm, v(-4.1, -23.03) * mm]});
            skLineSegment(sketch, "E313", {"start": v(-3.64, -21.9) * mm, "end": v(-3.57, -22.29) * mm});
            skLineSegment(sketch, "E314", {"start": v(-3.57, -22.29) * mm, "end": v(-3.8, -22.53) * mm});
            skFitSpline(sketch, "E315", {"points": [v(-4.17, -23.3) * mm, v(-4.2, -23.04) * mm, v(-4.21, -22.78) * mm, v(-4.23, -22.51) * mm]});
            skFitSpline(sketch, "E316", {"points": [v(-4.23, -22.51) * mm, v(-4.42, -22.26) * mm, v(-4.64, -22) * mm, v(-4.75, -21.7) * mm]});
            skFitSpline(sketch, "E317", {"points": [v(-4.75, -21.7) * mm, v(-4.85, -21.45) * mm, v(-5.06, -21.38) * mm, v(-5.18, -21.57) * mm]});
            skFitSpline(sketch, "E318", {"points": [v(-5.18, -21.57) * mm, v(-5.34, -22.12) * mm, v(-5.27, -22.63) * mm, v(-5.42, -23.21) * mm]});
            skFitSpline(sketch, "E319", {"points": [v(-5.42, -23.21) * mm, v(-5.44, -23.31) * mm, v(-5.47, -23.42) * mm, v(-5.47, -23.45) * mm]});
            skFitSpline(sketch, "E320", {"points": [v(-5.47, -23.45) * mm, v(-5.47, -23.48) * mm, v(-5.56, -23.53) * mm, v(-5.66, -23.55) * mm]});
            skFitSpline(sketch, "E321", {"points": [v(-5.66, -23.55) * mm, v(-5.75, -23.58) * mm, v(-5.87, -23.7) * mm, v(-5.92, -23.83) * mm]});
            skFitSpline(sketch, "E322", {"points": [v(-5.92, -23.83) * mm, v(-6.07, -24.2) * mm, v(-6.18, -24.1) * mm, v(-6.24, -23.55) * mm]});
            skLineSegment(sketch, "E323", {"start": v(-4.1, -23.03) * mm, "end": v(-4.17, -23.3) * mm});
            skFitSpline(sketch, "E324", {"points": [v(-5.62, -22.88) * mm, v(-5.53, -22.63) * mm, v(-5.42, -22) * mm, v(-5.37, -21.5) * mm]});
            skFitSpline(sketch, "E325", {"points": [v(-5.37, -21.5) * mm, v(-5.31, -20.98) * mm, v(-5.24, -20.56) * mm, v(-5.2, -20.56) * mm]});
            skFitSpline(sketch, "E326", {"points": [v(-5.2, -20.56) * mm, v(-4.79, -20.88) * mm, v(-4.39, -21.2) * mm, v(-4.29, -21.76) * mm]});
            skFitSpline(sketch, "E327", {"points": [v(-4.29, -21.76) * mm, v(-4.25, -21.98) * mm, v(-4.2, -22.15) * mm, v(-4.04, -22.3) * mm]});
            skFitSpline(sketch, "E328", {"points": [v(-4.04, -22.3) * mm, v(-3.97, -22.23) * mm, v(-3.9, -22.16) * mm, v(-3.82, -22.09) * mm]});
            skLineSegment(sketch, "E329", {"start": v(-6.24, -23.55) * mm, "end": v(-6.24, -23.55) * mm});
            skFitSpline(sketch, "E330", {"points": [v(-4.37, -20.57) * mm, v(-4.55, -20.38) * mm, v(-4.74, -20.08) * mm, v(-5, -20.03) * mm]});
            skFitSpline(sketch, "E331", {"points": [v(-5, -20.03) * mm, v(-5.08, -20.03) * mm, v(-5.24, -19.94) * mm, v(-5.36, -19.85) * mm]});
            skFitSpline(sketch, "E332", {"points": [v(-5.36, -19.85) * mm, v(-5.49, -19.75) * mm, v(-5.69, -19.67) * mm, v(-5.8, -19.67) * mm]});
            skFitSpline(sketch, "E333", {"points": [v(-5.8, -19.67) * mm, v(-6.06, -19.63) * mm, v(-6.19, -19.48) * mm, v(-6.35, -19.3) * mm]});
            skFitSpline(sketch, "E334", {"points": [v(-6.35, -19.3) * mm, v(-6.43, -19.65) * mm, v(-6.54, -20.01) * mm, v(-6.62, -20.31) * mm]});
            skFitSpline(sketch, "E335", {"points": [v(-6.62, -20.31) * mm, v(-6.72, -20.65) * mm, v(-6.78, -20.94) * mm, v(-6.75, -20.97) * mm]});
            skFitSpline(sketch, "E336", {"points": [v(-6.75, -20.97) * mm, v(-6.5, -20.85) * mm, v(-6.4, -20.65) * mm, v(-6.2, -20.43) * mm]});
            skFitSpline(sketch, "E337", {"points": [v(-6.2, -20.43) * mm, v(-6.14, -20.6) * mm, v(-6.08, -20.78) * mm, v(-6.01, -20.95) * mm]});
            skLineSegment(sketch, "E338", {"start": v(-3.82, -22.09) * mm, "end": v(-4.08, -21.32) * mm});
            skLineSegment(sketch, "E339", {"start": v(-4.08, -21.32) * mm, "end": v(-4.37, -20.57) * mm});
            skFitSpline(sketch, "E340", {"points": [v(-6.07, -22.05) * mm, v(-6.1, -22.66) * mm, v(-6.1, -23.22) * mm, v(-6.08, -23.3) * mm]});
            skFitSpline(sketch, "E341", {"points": [v(-6.08, -23.3) * mm, v(-5.99, -23.54) * mm, v(-5.8, -23.36) * mm, v(-5.62, -22.88) * mm]});
            skLineSegment(sketch, "E342", {"start": v(-6.01, -20.95) * mm, "end": v(-6.07, -22.05) * mm});
            skFitSpline(sketch, "E343", {"points": [v(2.7, -21.7) * mm, v(2.7, -21.5) * mm, v(2.2, -20.74) * mm, v(2.08, -20.74) * mm]});
            skFitSpline(sketch, "E344", {"points": [v(2.08, -20.74) * mm, v(2.04, -20.74) * mm, v(1.68, -20.5) * mm, v(1.27, -20.2) * mm]});
            skLineSegment(sketch, "E345", {"start": v(-5.62, -22.88) * mm, "end": v(-5.62, -22.88) * mm});
            skFitSpline(sketch, "E346", {"points": [v(-0.67, -19.54) * mm, v(-0.85, -19.61) * mm, v(-0.85, -19.73) * mm, v(-0.66, -19.83) * mm]});
            skLineSegment(sketch, "E347", {"start": v(1.27, -20.2) * mm, "end": v(0.54, -19.66) * mm});
            skLineSegment(sketch, "E348", {"start": v(0.54, -19.66) * mm, "end": v(0.31, -19.81) * mm});
            skLineSegment(sketch, "E349", {"start": v(0.31, -19.81) * mm, "end": v(0.1, -19.96) * mm});
            skLineSegment(sketch, "E350", {"start": v(0.1, -19.96) * mm, "end": v(-0.22, -19.72) * mm});
            skLineSegment(sketch, "E351", {"start": v(-0.22, -19.72) * mm, "end": v(-0.52, -19.49) * mm});
            skLineSegment(sketch, "E352", {"start": v(-0.52, -19.49) * mm, "end": v(-0.67, -19.54) * mm});
            skFitSpline(sketch, "E353", {"points": [v(-0.06, -20.9) * mm, v(0.1, -20.5) * mm, v(0.2, -20.45) * mm, v(0.48, -20.57) * mm]});
            skLineSegment(sketch, "E354", {"start": v(-0.66, -19.83) * mm, "end": v(-0.5, -19.91) * mm});
            skLineSegment(sketch, "E355", {"start": v(-0.5, -19.91) * mm, "end": v(-0.46, -20.52) * mm});
            skLineSegment(sketch, "E356", {"start": v(-0.46, -20.52) * mm, "end": v(-0.4, -21.13) * mm});
            skLineSegment(sketch, "E357", {"start": v(-0.4, -21.13) * mm, "end": v(-0.3, -21.17) * mm});
            skLineSegment(sketch, "E358", {"start": v(-0.3, -21.17) * mm, "end": v(-0.19, -21.2) * mm});
            skLineSegment(sketch, "E359", {"start": v(-0.19, -21.2) * mm, "end": v(-0.06, -20.9) * mm});
            skFitSpline(sketch, "E360", {"points": [v(0.9, -21.11) * mm, v(1.02, -21.35) * mm, v(1.18, -21.62) * mm, v(1.27, -21.7) * mm]});
            skLineSegment(sketch, "E361", {"start": v(0.48, -20.57) * mm, "end": v(0.7, -20.67) * mm});
            skLineSegment(sketch, "E362", {"start": v(0.7, -20.67) * mm, "end": v(0.9, -21.11) * mm});
            skFitSpline(sketch, "E363", {"points": [v(1.49, -21.71) * mm, v(1.51, -21.64) * mm, v(1.5, -21.48) * mm, v(1.45, -21.35) * mm]});
            skLineSegment(sketch, "E364", {"start": v(1.27, -21.7) * mm, "end": v(1.44, -21.85) * mm});
            skLineSegment(sketch, "E365", {"start": v(1.44, -21.85) * mm, "end": v(1.49, -21.71) * mm});
            skFitSpline(sketch, "E366", {"points": [v(1.47, -21.08) * mm, v(1.66, -21.01) * mm, v(2.11, -21.29) * mm, v(2.33, -21.6) * mm]});
            skFitSpline(sketch, "E367", {"points": [v(2.33, -21.6) * mm, v(2.57, -21.96) * mm, v(2.7, -22) * mm, v(2.7, -21.7) * mm]});
            skLineSegment(sketch, "E368", {"start": v(1.45, -21.35) * mm, "end": v(1.36, -21.11) * mm});
            skLineSegment(sketch, "E369", {"start": v(1.36, -21.11) * mm, "end": v(1.47, -21.08) * mm});
            skFitSpline(sketch, "E370", {"points": [v(0.48, -9.2) * mm, v(0.79, -8.81) * mm, v(0.99, -8.35) * mm, v(0.99, -8.03) * mm]});
            skFitSpline(sketch, "E371", {"points": [v(0.8, -7.84) * mm, v(0.49, -7.92) * mm, v(0.65, -7.74) * mm, v(1.17, -7.43) * mm]});
            skLineSegment(sketch, "E372", {"start": v(0.99, -8.03) * mm, "end": v(0.99, -7.79) * mm});
            skLineSegment(sketch, "E373", {"start": v(0.99, -7.79) * mm, "end": v(0.8, -7.84) * mm});
            skFitSpline(sketch, "E374", {"points": [v(2, -4.44) * mm, v(1.85, -4.14) * mm, v(1.64, -3.82) * mm, v(1.53, -3.72) * mm]});
            skLineSegment(sketch, "E375", {"start": v(1.17, -7.43) * mm, "end": v(1.66, -7.13) * mm});
            skLineSegment(sketch, "E376", {"start": v(1.66, -7.13) * mm, "end": v(1.91, -6.64) * mm});
            skLineSegment(sketch, "E377", {"start": v(1.91, -6.64) * mm, "end": v(2.16, -6.14) * mm});
            skLineSegment(sketch, "E378", {"start": v(2.16, -6.14) * mm, "end": v(2.22, -5.56) * mm});
            skLineSegment(sketch, "E379", {"start": v(2.22, -5.56) * mm, "end": v(2.27, -4.97) * mm});
            skLineSegment(sketch, "E380", {"start": v(2.27, -4.97) * mm, "end": v(2, -4.44) * mm});
            skFitSpline(sketch, "E381", {"points": [v(1.4, -4.13) * mm, v(1.43, -4.45) * mm, v(1.51, -4.8) * mm, v(1.58, -4.9) * mm]});
            skLineSegment(sketch, "E382", {"start": v(1.53, -3.72) * mm, "end": v(1.34, -3.55) * mm});
            skLineSegment(sketch, "E383", {"start": v(1.34, -3.55) * mm, "end": v(1.4, -4.13) * mm});
            skFitSpline(sketch, "E384", {"points": [v(0.85, -7.05) * mm, v(0.75, -7.05) * mm, v(0.59, -7.1) * mm, v(0.48, -7.16) * mm]});
            skFitSpline(sketch, "E385", {"points": [v(0.48, -7.16) * mm, v(0.17, -7.33) * mm, v(0.11, -7.3) * mm, v(-0.08, -6.86) * mm]});
            skFitSpline(sketch, "E386", {"points": [v(-0.08, -6.86) * mm, v(-0.18, -6.64) * mm, v(-0.44, -6.22) * mm, v(-0.67, -5.93) * mm]});
            skFitSpline(sketch, "E387", {"points": [v(-0.67, -5.93) * mm, v(-0.9, -5.64) * mm, v(-1.08, -5.34) * mm, v(-1.08, -5.28) * mm]});
            skLineSegment(sketch, "E388", {"start": v(1.58, -4.9) * mm, "end": v(1.7, -5.1) * mm});
            skLineSegment(sketch, "E389", {"start": v(1.7, -5.1) * mm, "end": v(1.61, -5.67) * mm});
            skLineSegment(sketch, "E390", {"start": v(1.61, -5.67) * mm, "end": v(1.52, -6.24) * mm});
            skLineSegment(sketch, "E391", {"start": v(1.52, -6.24) * mm, "end": v(1.27, -6.64) * mm});
            skLineSegment(sketch, "E392", {"start": v(1.27, -6.64) * mm, "end": v(1.03, -7.04) * mm});
            skLineSegment(sketch, "E393", {"start": v(1.03, -7.04) * mm, "end": v(0.85, -7.05) * mm});
            skFitSpline(sketch, "E394", {"points": [v(-1.68, -4.88) * mm, v(-2.02, -4.72) * mm, v(-2.4, -4.57) * mm, v(-2.54, -4.54) * mm]});
            skLineSegment(sketch, "E395", {"start": v(-1.08, -5.28) * mm, "end": v(-1.08, -5.16) * mm});
            skLineSegment(sketch, "E396", {"start": v(-1.08, -5.16) * mm, "end": v(-1.68, -4.88) * mm});
            skFitSpline(sketch, "E397", {"points": [v(-2.69, -4.64) * mm, v(-2.63, -4.73) * mm, v(-2.47, -4.87) * mm, v(-2.32, -4.96) * mm]});
            skFitSpline(sketch, "E398", {"points": [v(-2.32, -4.96) * mm, v(-2.18, -5.04) * mm, v(-2.06, -5.15) * mm, v(-2.06, -5.2) * mm]});
            skLineSegment(sketch, "E399", {"start": v(-2.54, -4.54) * mm, "end": v(-2.79, -4.48) * mm});
            skLineSegment(sketch, "E400", {"start": v(-2.79, -4.48) * mm, "end": v(-2.69, -4.64) * mm});
            skFitSpline(sketch, "E401", {"points": [v(-2.27, -5.25) * mm, v(-2.38, -5.22) * mm, v(-2.62, -5.17) * mm, v(-2.8, -5.14) * mm]});
            skLineSegment(sketch, "E402", {"start": v(-2.06, -5.2) * mm, "end": v(-2.06, -5.31) * mm});
            skLineSegment(sketch, "E403", {"start": v(-2.06, -5.31) * mm, "end": v(-2.27, -5.25) * mm});
            skFitSpline(sketch, "E404", {"points": [v(-3.14, -5.18) * mm, v(-3.14, -5.28) * mm, v(-2.5, -5.56) * mm, v(-2.26, -5.56) * mm]});
            skFitSpline(sketch, "E405", {"points": [v(-2.26, -5.56) * mm, v(-2, -5.56) * mm, v(-1.5, -5.91) * mm, v(-0.92, -6.5) * mm]});
            skLineSegment(sketch, "E406", {"start": v(-2.8, -5.14) * mm, "end": v(-3.14, -5.09) * mm});
            skLineSegment(sketch, "E407", {"start": v(-3.14, -5.09) * mm, "end": v(-3.14, -5.18) * mm});
            skFitSpline(sketch, "E408", {"points": [v(-0.22, -7.55) * mm, v(-0.14, -7.82) * mm, v(-0.05, -8.37) * mm, v(-0.02, -8.77) * mm]});
            skLineSegment(sketch, "E409", {"start": v(-0.92, -6.5) * mm, "end": v(-0.37, -7.07) * mm});
            skLineSegment(sketch, "E410", {"start": v(-0.37, -7.07) * mm, "end": v(-0.22, -7.55) * mm});
            skFitSpline(sketch, "E411", {"points": [v(0.13, -9.51) * mm, v(0.18, -9.51) * mm, v(0.34, -9.37) * mm, v(0.48, -9.2) * mm]});
            skLineSegment(sketch, "E412", {"start": v(-0.02, -8.77) * mm, "end": v(0.02, -9.51) * mm});
            skLineSegment(sketch, "E413", {"start": v(0.02, -9.51) * mm, "end": v(0.13, -9.51) * mm});
            skFitSpline(sketch, "E414", {"points": [v(-0.34, -8.12) * mm, v(-0.36, -7.95) * mm, v(-0.4, -7.8) * mm, v(-0.43, -7.81) * mm]});
            skFitSpline(sketch, "E415", {"points": [v(-0.43, -7.81) * mm, v(-0.55, -7.82) * mm, v(-0.8, -8.05) * mm, v(-0.8, -8.15) * mm]});
            skFitSpline(sketch, "E416", {"points": [v(-0.8, -8.15) * mm, v(-0.8, -8.25) * mm, v(-0.56, -8.43) * mm, v(-0.4, -8.43) * mm]});
            skLineSegment(sketch, "E417", {"start": v(-0.4, -8.43) * mm, "end": v(-0.3, -8.44) * mm});
            skLineSegment(sketch, "E418", {"start": v(-0.3, -8.44) * mm, "end": v(-0.34, -8.12) * mm});
            skLineSegment(sketch, "E419", {"start": v(-0.34, -8.12) * mm, "end": v(-0.34, -8.12) * mm});
            skFitSpline(sketch, "E420", {"points": [v(-0.9, -7.18) * mm, v(-0.94, -7.18) * mm, v(-0.99, -7.08) * mm, v(-0.99, -6.96) * mm]});
            skFitSpline(sketch, "E421", {"points": [v(-0.99, -6.96) * mm, v(-0.99, -6.8) * mm, v(-1.18, -6.46) * mm, v(-1.29, -6.46) * mm]});
            skFitSpline(sketch, "E422", {"points": [v(-1.29, -6.46) * mm, v(-1.3, -6.46) * mm, v(-1.44, -6.42) * mm, v(-1.6, -6.37) * mm]});
            skLineSegment(sketch, "E423", {"start": v(-0.9, -7.35) * mm, "end": v(-0.8, -7.18) * mm});
            skLineSegment(sketch, "E424", {"start": v(-0.8, -7.18) * mm, "end": v(-0.9, -7.18) * mm});
            skFitSpline(sketch, "E425", {"points": [v(-1.21, -7.56) * mm, v(-1.09, -7.54) * mm, v(-0.94, -7.44) * mm, v(-0.9, -7.35) * mm]});
            skLineSegment(sketch, "E426", {"start": v(-1.6, -6.37) * mm, "end": v(-1.92, -6.28) * mm});
            skLineSegment(sketch, "E427", {"start": v(-1.92, -6.28) * mm, "end": v(-1.62, -6.59) * mm});
            skLineSegment(sketch, "E428", {"start": v(-1.62, -6.59) * mm, "end": v(-1.33, -6.9) * mm});
            skLineSegment(sketch, "E429", {"start": v(-1.33, -6.9) * mm, "end": v(-1.39, -7.08) * mm});
            skLineSegment(sketch, "E430", {"start": v(-1.39, -7.08) * mm, "end": v(-1.45, -7.27) * mm});
            skLineSegment(sketch, "E431", {"start": v(-1.45, -7.27) * mm, "end": v(-1.64, -7.27) * mm});
            skLineSegment(sketch, "E432", {"start": v(-1.64, -7.27) * mm, "end": v(-1.84, -7.28) * mm});
            skLineSegment(sketch, "E433", {"start": v(-1.84, -7.28) * mm, "end": v(-1.64, -7.44) * mm});
            skLineSegment(sketch, "E434", {"start": v(-1.64, -7.44) * mm, "end": v(-1.44, -7.6) * mm});
            skLineSegment(sketch, "E435", {"start": v(-1.44, -7.6) * mm, "end": v(-1.21, -7.56) * mm});
            skFitSpline(sketch, "E436", {"points": [v(-2.45, -6.93) * mm, v(-2.54, -6.83) * mm, v(-2.7, -6.5) * mm, v(-2.84, -6.18) * mm]});
            skFitSpline(sketch, "E437", {"points": [v(-2.84, -6.18) * mm, v(-3.07, -5.61) * mm, v(-3.17, -5.48) * mm, v(-3.39, -5.47) * mm]});
            skLineSegment(sketch, "E438", {"start": v(-0.9, -7.35) * mm, "end": v(-0.9, -7.35) * mm});
            skFitSpline(sketch, "E439", {"points": [v(-3.17, -6.6) * mm, v(-2.7, -6.98) * mm, v(-2.4, -7.18) * mm, v(-2.35, -7.13) * mm]});
            skFitSpline(sketch, "E440", {"points": [v(-2.35, -7.13) * mm, v(-2.32, -7.1) * mm, v(-2.37, -7.02) * mm, v(-2.45, -6.93) * mm]});
            skLineSegment(sketch, "E441", {"start": v(-3.39, -5.47) * mm, "end": v(-3.5, -5.47) * mm});
            skLineSegment(sketch, "E442", {"start": v(-3.5, -5.47) * mm, "end": v(-3.5, -5.9) * mm});
            skLineSegment(sketch, "E443", {"start": v(-3.5, -5.9) * mm, "end": v(-3.5, -6.33) * mm});
            skLineSegment(sketch, "E444", {"start": v(-3.5, -6.33) * mm, "end": v(-3.17, -6.6) * mm});
            skFitSpline(sketch, "E445", {"points": [v(-6, -2.71) * mm, v(-6.02, -2.62) * mm, v(-6.27, -2.11) * mm, v(-6.55, -1.57) * mm]});
            skFitSpline(sketch, "E446", {"points": [v(-7.32, -0.43) * mm, v(-7.47, -0.34) * mm, v(-7.73, -0.19) * mm, v(-7.9, -0.1) * mm]});
            skFitSpline(sketch, "E447", {"points": [v(-7.9, -0.1) * mm, v(-8.09, 0) * mm, v(-8.28, 0.15) * mm, v(-8.35, 0.23) * mm]});
            skFitSpline(sketch, "E448", {"points": [v(-8.35, 0.23) * mm, v(-8.42, 0.31) * mm, v(-8.65, 0.48) * mm, v(-8.86, 0.6) * mm]});
            skFitSpline(sketch, "E449", {"points": [v(-8.86, 0.6) * mm, v(-9.28, 0.85) * mm, v(-9.34, 0.96) * mm, v(-9.1, 1.01) * mm]});
            skLineSegment(sketch, "E450", {"start": v(-6.55, -1.57) * mm, "end": v(-7.06, -0.59) * mm});
            skLineSegment(sketch, "E451", {"start": v(-7.06, -0.59) * mm, "end": v(-7.32, -0.43) * mm});
            skFitSpline(sketch, "E452", {"points": [v(-9.56, 1.44) * mm, v(-10.2, 1.86) * mm, v(-10.99, 2.25) * mm, v(-11.18, 2.25) * mm]});
            skFitSpline(sketch, "E453", {"points": [v(-11.18, 2.25) * mm, v(-11.34, 2.25) * mm, v(-11.53, 2.5) * mm, v(-11.46, 2.6) * mm]});
            skLineSegment(sketch, "E454", {"start": v(-9.1, 1.01) * mm, "end": v(-8.95, 1.04) * mm});
            skLineSegment(sketch, "E455", {"start": v(-8.95, 1.04) * mm, "end": v(-9.56, 1.44) * mm});
            skFitSpline(sketch, "E456", {"points": [v(-10.89, 2.47) * mm, v(-10.13, 2.14) * mm, v(-8.98, 1.54) * mm, v(-8.65, 1.3) * mm]});
            skFitSpline(sketch, "E457", {"points": [v(-8.65, 1.3) * mm, v(-8.5, 1.18) * mm, v(-8.34, 1.09) * mm, v(-8.3, 1.09) * mm]});
            skFitSpline(sketch, "E458", {"points": [v(-8.3, 1.09) * mm, v(-8.18, 1.09) * mm, v(-6.95, 0.51) * mm, v(-6.7, 0.35) * mm]});
            skFitSpline(sketch, "E459", {"points": [v(-6.7, 0.35) * mm, v(-6.36, 0.1) * mm, v(-6.32, 0.2) * mm, v(-6.66, 0.46) * mm]});
            skFitSpline(sketch, "E460", {"points": [v(-6.66, 0.46) * mm, v(-6.8, 0.58) * mm, v(-7.14, 0.88) * mm, v(-7.4, 1.13) * mm]});
            skFitSpline(sketch, "E461", {"points": [v(-7.4, 1.13) * mm, v(-9.28, 2.96) * mm, v(-9.92, 3.31) * mm, v(-12.35, 3.9) * mm]});
            skFitSpline(sketch, "E462", {"points": [v(-12.35, 3.9) * mm, v(-12.84, 4.03) * mm, v(-13.6, 4.15) * mm, v(-14.01, 4.18) * mm]});
            skFitSpline(sketch, "E463", {"points": [v(-14.01, 4.18) * mm, v(-15.47, 4.3) * mm, v(-17.5, 4.71) * mm, v(-19.94, 5.4) * mm]});
            skFitSpline(sketch, "E464", {"points": [v(-19.94, 5.4) * mm, v(-20.63, 5.6) * mm, v(-20.94, 5.68) * mm, v(-21.65, 5.83) * mm]});
            skFitSpline(sketch, "E465", {"points": [v(-21.65, 5.83) * mm, v(-22.59, 6.03) * mm, v(-24.51, 6.57) * mm, v(-24.97, 6.75) * mm]});
            skFitSpline(sketch, "E466", {"points": [v(-24.97, 6.75) * mm, v(-25.24, 6.86) * mm, v(-25.63, 7) * mm, v(-25.82, 7.06) * mm]});
            skFitSpline(sketch, "E467", {"points": [v(-25.82, 7.06) * mm, v(-26.72, 7.33) * mm, v(-27.67, 7.8) * mm, v(-28.77, 8.5) * mm]});
            skFitSpline(sketch, "E468", {"points": [v(-28.77, 8.5) * mm, v(-29.66, 9.08) * mm, v(-29.81, 9.17) * mm, v(-29.86, 9.17) * mm]});
            skFitSpline(sketch, "E469", {"points": [v(-29.86, 9.17) * mm, v(-29.9, 9.17) * mm, v(-28.8, 8.1) * mm, v(-28.42, 7.78) * mm]});
            skFitSpline(sketch, "E470", {"points": [v(-28.42, 7.78) * mm, v(-27.73, 7.13) * mm, v(-26.81, 6.7) * mm, v(-26.06, 6.24) * mm]});
            skLineSegment(sketch, "E471", {"start": v(-11.46, 2.6) * mm, "end": v(-11.4, 2.7) * mm});
            skLineSegment(sketch, "E472", {"start": v(-11.4, 2.7) * mm, "end": v(-10.89, 2.47) * mm});
            skFitSpline(sketch, "E473", {"points": [v(-26.18, 6.48) * mm, v(-26.38, 6.85) * mm, v(-26.26, 6.78) * mm, v(-25.44, 6.45) * mm]});
            skFitSpline(sketch, "E474", {"points": [v(-25.44, 6.45) * mm, v(-25.01, 6.28) * mm, v(-24.56, 6.11) * mm, v(-24.43, 6.09) * mm]});
            skFitSpline(sketch, "E475", {"points": [v(-24.43, 6.09) * mm, v(-24.11, 6.02) * mm, v(-23.51, 5.8) * mm, v(-22.85, 5.48) * mm]});
            skFitSpline(sketch, "E476", {"points": [v(-22.85, 5.48) * mm, v(-21.7, 4.95) * mm, v(-18.37, 3.77) * mm, v(-17.38, 3.55) * mm]});
            skFitSpline(sketch, "E477", {"points": [v(-17.38, 3.55) * mm, v(-16.28, 3.3) * mm, v(-14.37, 2.96) * mm, v(-13.43, 2.82) * mm]});
            skLineSegment(sketch, "E478", {"start": v(-26.06, 6.24) * mm, "end": v(-26.18, 6.48) * mm});
            skFitSpline(sketch, "E479", {"points": [v(-12.09, 2.32) * mm, v(-11.19, 1.88) * mm, v(-10.74, 1.57) * mm, v(-10.16, 1.01) * mm]});
            skFitSpline(sketch, "E480", {"points": [v(-10.16, 1.01) * mm, v(-9.99, 0.85) * mm, v(-9.66, 0.58) * mm, v(-9.42, 0.43) * mm]});
            skFitSpline(sketch, "E481", {"points": [v(-9.42, 0.43) * mm, v(-9.19, 0.27) * mm, v(-8.73, -0.04) * mm, v(-8.41, -0.26) * mm]});
            skLineSegment(sketch, "E482", {"start": v(-13.43, 2.82) * mm, "end": v(-12.99, 2.76) * mm});
            skLineSegment(sketch, "E483", {"start": v(-12.99, 2.76) * mm, "end": v(-12.09, 2.32) * mm});
            skFitSpline(sketch, "E484", {"points": [v(-6.61, -2.35) * mm, v(-6.03, -2.89) * mm, v(-5.9, -2.97) * mm, v(-6, -2.71) * mm]});
            skLineSegment(sketch, "E485", {"start": v(-8.41, -0.26) * mm, "end": v(-7.83, -0.67) * mm});
            skLineSegment(sketch, "E486", {"start": v(-7.83, -0.67) * mm, "end": v(-7.5, -1.25) * mm});
            skLineSegment(sketch, "E487", {"start": v(-7.5, -1.25) * mm, "end": v(-7.16, -1.83) * mm});
            skLineSegment(sketch, "E488", {"start": v(-7.16, -1.83) * mm, "end": v(-6.61, -2.35) * mm});
            skFitSpline(sketch, "E489", {"points": [v(1.28, -2.05) * mm, v(1.69, -1.9) * mm, v(2.15, -1.75) * mm, v(2.3, -1.7) * mm]});
            skFitSpline(sketch, "E490", {"points": [v(2.3, -1.7) * mm, v(2.47, -1.66) * mm, v(2.7, -1.54) * mm, v(2.85, -1.43) * mm]});
            skFitSpline(sketch, "E491", {"points": [v(2.85, -1.43) * mm, v(2.99, -1.32) * mm, v(3.24, -1.18) * mm, v(3.4, -1.1) * mm]});
            skFitSpline(sketch, "E492", {"points": [v(3.4, -1.1) * mm, v(3.57, -1.04) * mm, v(3.85, -0.87) * mm, v(4.03, -0.73) * mm]});
            skFitSpline(sketch, "E493", {"points": [v(4.03, -0.73) * mm, v(4.21, -0.58) * mm, v(4.48, -0.4) * mm, v(4.63, -0.32) * mm]});
            skFitSpline(sketch, "E494", {"points": [v(4.63, -0.32) * mm, v(4.78, -0.24) * mm, v(5.06, -0.05) * mm, v(5.26, 0.1) * mm]});
            skFitSpline(sketch, "E495", {"points": [v(6.33, 0.55) * mm, v(6.73, 0.66) * mm, v(7.25, 0.78) * mm, v(7.49, 0.82) * mm]});
            skLineSegment(sketch, "E496", {"start": v(5.26, 0.1) * mm, "end": v(5.62, 0.36) * mm});
            skLineSegment(sketch, "E497", {"start": v(5.62, 0.36) * mm, "end": v(6.33, 0.55) * mm});
            skFitSpline(sketch, "E498", {"points": [v(9.13, 1.02) * mm, v(10.61, 1.61) * mm, v(11.86, 1.77) * mm, v(15.54, 1.83) * mm]});
            skLineSegment(sketch, "E499", {"start": v(7.49, 0.82) * mm, "end": v(7.92, 0.9) * mm});
            skLineSegment(sketch, "E500", {"start": v(7.92, 0.9) * mm, "end": v(8.13, 0.8) * mm});
            skLineSegment(sketch, "E501", {"start": v(8.13, 0.8) * mm, "end": v(8.33, 0.7) * mm});
            skLineSegment(sketch, "E502", {"start": v(8.33, 0.7) * mm, "end": v(9.13, 1.02) * mm});
            skFitSpline(sketch, "E503", {"points": [v(18.64, 2.03) * mm, v(19.09, 2.12) * mm, v(20, 2.37) * mm, v(20.69, 2.58) * mm]});
            skFitSpline(sketch, "E504", {"points": [v(20.69, 2.58) * mm, v(21.37, 2.8) * mm, v(22.23, 3.02) * mm, v(22.62, 3.06) * mm]});
            skFitSpline(sketch, "E505", {"points": [v(22.62, 3.06) * mm, v(23.6, 3.18) * mm, v(24.36, 3.38) * mm, v(24.49, 3.55) * mm]});
            skLineSegment(sketch, "E506", {"start": v(15.54, 1.83) * mm, "end": v(17.83, 1.87) * mm});
            skLineSegment(sketch, "E507", {"start": v(17.83, 1.87) * mm, "end": v(18.64, 2.03) * mm});
            skFitSpline(sketch, "E508", {"points": [v(27.18, 4.09) * mm, v(27.72, 4.26) * mm, v(28.26, 4.4) * mm, v(28.38, 4.4) * mm]});
            skFitSpline(sketch, "E509", {"points": [v(28.38, 4.4) * mm, v(28.5, 4.4) * mm, v(28.92, 4.47) * mm, v(29.3, 4.55) * mm]});
            skLineSegment(sketch, "E510", {"start": v(24.49, 3.55) * mm, "end": v(24.59, 3.69) * mm});
            skLineSegment(sketch, "E511", {"start": v(24.59, 3.69) * mm, "end": v(25.39, 3.73) * mm});
            skLineSegment(sketch, "E512", {"start": v(25.39, 3.73) * mm, "end": v(26.19, 3.76) * mm});
            skLineSegment(sketch, "E513", {"start": v(26.19, 3.76) * mm, "end": v(27.18, 4.09) * mm});
            skFitSpline(sketch, "E514", {"points": [v(30.02, 4.7) * mm, v(30.13, 4.66) * mm, v(30.14, 4.58) * mm, v(30.2, 4.52) * mm]});
            skLineSegment(sketch, "E515", {"start": v(29.3, 4.55) * mm, "end": v(30.02, 4.7) * mm});
            skFitSpline(sketch, "E516", {"points": [v(30.8, 4.73) * mm, v(31.13, 4.84) * mm, v(31.56, 5) * mm, v(31.76, 5.07) * mm]});
            skFitSpline(sketch, "E517", {"points": [v(31.76, 5.07) * mm, v(31.95, 5.15) * mm, v(32.25, 5.21) * mm, v(32.4, 5.21) * mm]});
            skLineSegment(sketch, "E518", {"start": v(30.2, 4.52) * mm, "end": v(30.8, 4.73) * mm});
            skFitSpline(sketch, "E519", {"points": [v(33.2, 5.5) * mm, v(33.47, 5.65) * mm, v(33.69, 5.82) * mm, v(33.69, 5.88) * mm]});
            skLineSegment(sketch, "E520", {"start": v(32.4, 5.21) * mm, "end": v(32.7, 5.22) * mm});
            skLineSegment(sketch, "E521", {"start": v(32.7, 5.22) * mm, "end": v(33.2, 5.5) * mm});
            skFitSpline(sketch, "E522", {"points": [v(33, 5.92) * mm, v(32.2, 5.85) * mm, v(32.08, 5.7) * mm, v(31.17, 5.41) * mm]});
            skFitSpline(sketch, "E523", {"points": [v(31.17, 5.41) * mm, v(30.72, 5.3) * mm, v(32.84, 6.18) * mm, v(33.37, 6.34) * mm]});
            skFitSpline(sketch, "E524", {"points": [v(33.37, 6.34) * mm, v(33.67, 6.42) * mm, v(34.14, 6.63) * mm, v(34.42, 6.8) * mm]});
            skFitSpline(sketch, "E525", {"points": [v(34.42, 6.8) * mm, v(34.7, 6.97) * mm, v(34.96, 7.1) * mm, v(35, 7.1) * mm]});
            skFitSpline(sketch, "E526", {"points": [v(35, 7.1) * mm, v(35.05, 7.1) * mm, v(35.2, 7.2) * mm, v(35.34, 7.31) * mm]});
            skLineSegment(sketch, "E527", {"start": v(33.69, 5.88) * mm, "end": v(33.69, 5.99) * mm});
            skLineSegment(sketch, "E528", {"start": v(33.69, 5.99) * mm, "end": v(33, 5.92) * mm});
            skFitSpline(sketch, "E529", {"points": [v(35.14, 7.53) * mm, v(34.76, 7.3) * mm, v(34.19, 7.04) * mm, v(33.28, 6.7) * mm]});
            skFitSpline(sketch, "E530", {"points": [v(33.28, 6.7) * mm, v(32.94, 6.56) * mm, v(32.4, 6.35) * mm, v(32.07, 6.23) * mm]});
            skFitSpline(sketch, "E531", {"points": [v(32.07, 6.23) * mm, v(31.75, 6.1) * mm, v(31.36, 5.95) * mm, v(31.2, 5.88) * mm]});
            skFitSpline(sketch, "E532", {"points": [v(31.2, 5.88) * mm, v(30.02, 5.37) * mm, v(29.9, 5.33) * mm, v(29.02, 5.21) * mm]});
            skFitSpline(sketch, "E533", {"points": [v(29.02, 5.21) * mm, v(28.6, 5.16) * mm, v(27.87, 5.06) * mm, v(27.4, 5) * mm]});
            skFitSpline(sketch, "E534", {"points": [v(27.4, 5) * mm, v(25.75, 4.77) * mm, v(24.77, 4.5) * mm, v(24.63, 4.26) * mm]});
            skLineSegment(sketch, "E535", {"start": v(35.34, 7.31) * mm, "end": v(35.6, 7.52) * mm});
            skLineSegment(sketch, "E536", {"start": v(35.6, 7.52) * mm, "end": v(35.54, 7.63) * mm});
            skLineSegment(sketch, "E537", {"start": v(35.54, 7.63) * mm, "end": v(35.48, 7.73) * mm});
            skLineSegment(sketch, "E538", {"start": v(35.48, 7.73) * mm, "end": v(35.14, 7.53) * mm});
            skFitSpline(sketch, "E539", {"points": [v(23.53, 4.04) * mm, v(22.51, 3.95) * mm, v(22.1, 3.89) * mm, v(21.25, 3.69) * mm]});
            skFitSpline(sketch, "E540", {"points": [v(21.25, 3.69) * mm, v(21, 3.63) * mm, v(20.45, 3.5) * mm, v(20.03, 3.41) * mm]});
            skFitSpline(sketch, "E541", {"points": [v(20.03, 3.41) * mm, v(19.61, 3.32) * mm, v(18.95, 3.14) * mm, v(18.55, 3.02) * mm]});
            skFitSpline(sketch, "E542", {"points": [v(18.55, 3.02) * mm, v(17.6, 2.71) * mm, v(16.44, 2.54) * mm, v(14.69, 2.43) * mm]});
            skFitSpline(sketch, "E543", {"points": [v(14.69, 2.43) * mm, v(10.94, 2.2) * mm, v(10.26, 2.15) * mm, v(9.93, 2.07) * mm]});
            skFitSpline(sketch, "E544", {"points": [v(9.93, 2.07) * mm, v(9.46, 1.96) * mm, v(9.34, 1.96) * mm, v(9.34, 2.07) * mm]});
            skFitSpline(sketch, "E545", {"points": [v(9.34, 2.07) * mm, v(9.34, 2.16) * mm, v(9.79, 2.3) * mm, v(10.42, 2.38) * mm]});
            skFitSpline(sketch, "E546", {"points": [v(10.42, 2.38) * mm, v(10.64, 2.42) * mm, v(10.93, 2.5) * mm, v(11.05, 2.58) * mm]});
            skLineSegment(sketch, "E547", {"start": v(24.63, 4.26) * mm, "end": v(24.56, 4.14) * mm});
            skLineSegment(sketch, "E548", {"start": v(24.56, 4.14) * mm, "end": v(23.53, 4.04) * mm});
            skFitSpline(sketch, "E549", {"points": [v(10.6, 2.66) * mm, v(10.23, 2.63) * mm, v(9.83, 2.6) * mm, v(9.7, 2.58) * mm]});
            skFitSpline(sketch, "E550", {"points": [v(9.7, 2.58) * mm, v(9.58, 2.56) * mm, v(9.24, 2.52) * mm, v(8.94, 2.49) * mm]});
            skFitSpline(sketch, "E551", {"points": [v(8.94, 2.49) * mm, v(8.27, 2.41) * mm, v(7.79, 2.29) * mm, v(7.32, 2.08) * mm]});
            skFitSpline(sketch, "E552", {"points": [v(7.32, 2.08) * mm, v(7.13, 1.99) * mm, v(6.9, 1.89) * mm, v(6.83, 1.86) * mm]});
            skFitSpline(sketch, "E553", {"points": [v(6.83, 1.86) * mm, v(6.75, 1.83) * mm, v(6.53, 1.68) * mm, v(6.33, 1.53) * mm]});
            skFitSpline(sketch, "E554", {"points": [v(6.33, 1.53) * mm, v(6.14, 1.38) * mm, v(5.75, 1.11) * mm, v(5.48, 0.93) * mm]});
            skFitSpline(sketch, "E555", {"points": [v(5.48, 0.93) * mm, v(5.2, 0.74) * mm, v(4.74, 0.4) * mm, v(4.45, 0.19) * mm]});
            skFitSpline(sketch, "E556", {"points": [v(4.45, 0.19) * mm, v(4.15, -0.04) * mm, v(3.64, -0.34) * mm, v(3.32, -0.49) * mm]});
            skFitSpline(sketch, "E557", {"points": [v(3.32, -0.49) * mm, v(3, -0.64) * mm, v(2.72, -0.78) * mm, v(2.7, -0.8) * mm]});
            skFitSpline(sketch, "E558", {"points": [v(2.7, -0.8) * mm, v(2.5, -1) * mm, v(1.17, -1.47) * mm, v(0.43, -1.6) * mm]});
            skFitSpline(sketch, "E559", {"points": [v(0.43, -1.6) * mm, v(0.1, -1.67) * mm, v(-0.18, -1.74) * mm, v(-0.18, -1.77) * mm]});
            skFitSpline(sketch, "E560", {"points": [v(-0.18, -1.77) * mm, v(-0.18, -1.87) * mm, v(0.3, -2.33) * mm, v(0.42, -2.33) * mm]});
            skFitSpline(sketch, "E561", {"points": [v(0.42, -2.33) * mm, v(0.48, -2.33) * mm, v(0.86, -2.2) * mm, v(1.28, -2.05) * mm]});
            skLineSegment(sketch, "E562", {"start": v(11.05, 2.58) * mm, "end": v(11.28, 2.71) * mm});
            skLineSegment(sketch, "E563", {"start": v(11.28, 2.71) * mm, "end": v(10.6, 2.66) * mm});
            skFitSpline(sketch, "E564", {"points": [v(-24.25, -1.95) * mm, v(-24.42, -1.79) * mm, v(-24.72, -1.55) * mm, v(-24.92, -1.42) * mm]});
            skFitSpline(sketch, "E565", {"points": [v(-24.92, -1.42) * mm, v(-25.26, -1.2) * mm, v(-27.03, -0.44) * mm, v(-27.18, -0.44) * mm]});
            skFitSpline(sketch, "E566", {"points": [v(-27.18, -0.44) * mm, v(-27.22, -0.44) * mm, v(-27.12, -0.58) * mm, v(-26.95, -0.76) * mm]});
            skFitSpline(sketch, "E567", {"points": [v(-26.95, -0.76) * mm, v(-26.82, -1) * mm, v(-26.56, -1.09) * mm, v(-26.33, -1.24) * mm]});
            skFitSpline(sketch, "E568", {"points": [v(-26.33, -1.24) * mm, v(-26.16, -1.34) * mm, v(-25.18, -1.84) * mm, v(-24.67, -1.98) * mm]});
            skFitSpline(sketch, "E569", {"points": [v(-24.67, -1.98) * mm, v(-24.47, -2.04) * mm, v(-24.26, -2.12) * mm, v(-24.21, -2.16) * mm]});
            skFitSpline(sketch, "E570", {"points": [v(-24.21, -2.16) * mm, v(-24.17, -2.2) * mm, v(-24.08, -2.24) * mm, v(-24.03, -2.24) * mm]});
            skFitSpline(sketch, "E571", {"points": [v(-24.03, -2.24) * mm, v(-23.98, -2.24) * mm, v(-24.08, -2.1) * mm, v(-24.25, -1.95) * mm]});
            skLineSegment(sketch, "E572", {"start": v(1.28, -2.05) * mm, "end": v(1.28, -2.05) * mm});
            skFitSpline(sketch, "E573", {"points": [v(26.01, -1.53) * mm, v(26.55, -1.27) * mm, v(26.94, -0.94) * mm, v(26.83, -0.83) * mm]});
            skFitSpline(sketch, "E574", {"points": [v(26.83, -0.83) * mm, v(26.76, -0.76) * mm, v(26.05, -0.99) * mm, v(26.05, -1.09) * mm]});
            skFitSpline(sketch, "E575", {"points": [v(26.05, -1.09) * mm, v(26.05, -1.13) * mm, v(26, -1.16) * mm, v(25.92, -1.16) * mm]});
            skFitSpline(sketch, "E576", {"points": [v(25.92, -1.16) * mm, v(25.85, -1.16) * mm, v(25.74, -1.25) * mm, v(25.68, -1.36) * mm]});
            skFitSpline(sketch, "E577", {"points": [v(25.68, -1.36) * mm, v(25.62, -1.47) * mm, v(25.5, -1.61) * mm, v(25.43, -1.67) * mm]});
            skFitSpline(sketch, "E578", {"points": [v(25.43, -1.67) * mm, v(25.18, -1.87) * mm, v(25.47, -1.8) * mm, v(26.01, -1.53) * mm]});
            skFitSpline(sketch, "E579", {"points": [v(-4.31, -1.45) * mm, v(-4.31, -1.42) * mm, v(-4.61, -1.19) * mm, v(-4.98, -0.94) * mm]});
            skFitSpline(sketch, "E580", {"points": [v(-4.98, -0.94) * mm, v(-5.34, -0.7) * mm, v(-5.62, -0.46) * mm, v(-5.6, -0.4) * mm]});
            skFitSpline(sketch, "E581", {"points": [v(-5.6, -0.4) * mm, v(-5.57, -0.3) * mm, v(-6.1, 0.12) * mm, v(-6.18, 0.05) * mm]});
            skFitSpline(sketch, "E582", {"points": [v(-6.18, 0.05) * mm, v(-6.2, 0.03) * mm, v(-6.17, -0.17) * mm, v(-6.11, -0.38) * mm]});
            skFitSpline(sketch, "E583", {"points": [v(-5.63, -1) * mm, v(-4.82, -1.45) * mm, v(-4.3, -1.63) * mm, v(-4.31, -1.45) * mm]});
            skLineSegment(sketch, "E584", {"start": v(-6.11, -0.38) * mm, "end": v(-6, -0.78) * mm});
            skLineSegment(sketch, "E585", {"start": v(-6, -0.78) * mm, "end": v(-5.63, -1) * mm});
            skFitSpline(sketch, "E586", {"points": [v(28.09, 0.45) * mm, v(28.57, 0.7) * mm, v(29.3, 1.04) * mm, v(29.68, 1.21) * mm]});
            skFitSpline(sketch, "E587", {"points": [v(29.68, 1.21) * mm, v(30.07, 1.4) * mm, v(30.37, 1.56) * mm, v(30.34, 1.6) * mm]});
            skFitSpline(sketch, "E588", {"points": [v(30.34, 1.6) * mm, v(30.26, 1.67) * mm, v(28.85, 1.23) * mm, v(27.83, 0.8) * mm]});
            skFitSpline(sketch, "E589", {"points": [v(27.08, 0) * mm, v(27.14, 0) * mm, v(27.6, 0.2) * mm, v(28.09, 0.45) * mm]});
            skLineSegment(sketch, "E590", {"start": v(27.83, 0.8) * mm, "end": v(26.95, 0.43) * mm});
            skLineSegment(sketch, "E591", {"start": v(26.95, 0.43) * mm, "end": v(26.95, 0.22) * mm});
            skLineSegment(sketch, "E592", {"start": v(26.95, 0.22) * mm, "end": v(26.95, 0) * mm});
            skLineSegment(sketch, "E593", {"start": v(26.95, 0) * mm, "end": v(27.08, 0) * mm});
            skFitSpline(sketch, "E594", {"points": [v(31.62, 2.34) * mm, v(31.8, 2.43) * mm, v(32.22, 2.59) * mm, v(32.57, 2.7) * mm]});
            skFitSpline(sketch, "E595", {"points": [v(32.57, 2.7) * mm, v(33.36, 2.94) * mm, v(34.02, 3.26) * mm, v(33.96, 3.37) * mm]});
            skFitSpline(sketch, "E596", {"points": [v(33.96, 3.37) * mm, v(33.85, 3.57) * mm, v(32.5, 3.31) * mm, v(32.15, 3.03) * mm]});
            skFitSpline(sketch, "E597", {"points": [v(32.15, 3.03) * mm, v(31.9, 2.82) * mm, v(31.54, 2.6) * mm, v(30.96, 2.27) * mm]});
            skFitSpline(sketch, "E598", {"points": [v(30.94, 2.12) * mm, v(31.14, 2.15) * mm, v(31.44, 2.25) * mm, v(31.62, 2.34) * mm]});
            skLineSegment(sketch, "E599", {"start": v(30.96, 2.27) * mm, "end": v(30.59, 2.07) * mm});
            skLineSegment(sketch, "E600", {"start": v(30.59, 2.07) * mm, "end": v(30.94, 2.12) * mm});
            skFitSpline(sketch, "E601", {"points": [v(35.62, 5.08) * mm, v(35.77, 5.14) * mm, v(35.92, 5.2) * mm, v(36.02, 5.26) * mm]});
            skFitSpline(sketch, "E602", {"points": [v(35.14, 4.9) * mm, v(35.26, 4.94) * mm, v(35.47, 5.02) * mm, v(35.62, 5.08) * mm]});
            skLineSegment(sketch, "E603", {"start": v(36.02, 5.26) * mm, "end": v(35.97, 5.44) * mm});
            skLineSegment(sketch, "E604", {"start": v(35.97, 5.44) * mm, "end": v(35.57, 5.47) * mm});
            skLineSegment(sketch, "E605", {"start": v(35.57, 5.47) * mm, "end": v(35, 5.44) * mm});
            skLineSegment(sketch, "E606", {"start": v(35, 5.44) * mm, "end": v(34.96, 5.14) * mm});
            skLineSegment(sketch, "E607", {"start": v(34.96, 5.14) * mm, "end": v(34.93, 4.84) * mm});
            skLineSegment(sketch, "E608", {"start": v(34.93, 4.84) * mm, "end": v(35.14, 4.9) * mm});
            skFitSpline(sketch, "E609", {"points": [v(-31.11, 8.02) * mm, v(-31.4, 8.52) * mm, v(-32.09, 9.17) * mm, v(-33.11, 9.95) * mm]});
            skFitSpline(sketch, "E610", {"points": [v(-33.11, 9.95) * mm, v(-33.9, 10.54) * mm, v(-35.44, 11.4) * mm, v(-35.53, 11.3) * mm]});
            skFitSpline(sketch, "E611", {"points": [v(-35.53, 11.3) * mm, v(-35.63, 11.21) * mm, v(-33.82, 9.6) * mm, v(-33.03, 9.07) * mm]});
            skFitSpline(sketch, "E612", {"points": [v(-33.03, 9.07) * mm, v(-32.58, 8.76) * mm, v(-32.18, 8.48) * mm, v(-32.15, 8.44) * mm]});
            skFitSpline(sketch, "E613", {"points": [v(-32.15, 8.44) * mm, v(-32.08, 8.32) * mm, v(-30.95, 7.56) * mm, v(-30.92, 7.6) * mm]});
            skFitSpline(sketch, "E614", {"points": [v(-30.92, 7.6) * mm, v(-30.9, 7.61) * mm, v(-30.99, 7.8) * mm, v(-31.11, 8.02) * mm]});
            skSolve(sketch);
        }
        {
            var Q0;
            Q0=makeQuery(id+"F0.imprint","IMPRINT",FACE,{"disambiguationData":[TD([[makeQuery(id+"F0.imprint","IMPRINT",EDGE,{"derivedFrom":sQuery(id+"F0.wireOp",EDGE,"E0")}),-1.0]])]});
            extrude(context, id + "F1", {"entities" : qUnion([Q0]), "depth" : 3.17 * mm});
        }
        {
            var Q0;
            Q0=makeQuery(id+"F0.imprint","IMPRINT",FACE,{"disambiguationData":[TD([[makeQuery(id+"F0.imprint","IMPRINT",EDGE,{"derivedFrom":sQuery(id+"F0.wireOp",EDGE,"E445")}),1.0]])]});
            var Q1;
            Q1=makeQuery(id+"F0.imprint","IMPRINT",FACE,{"disambiguationData":[TD([[makeQuery(id+"F0.imprint","IMPRINT",EDGE,{"derivedFrom":sQuery(id+"F0.wireOp",EDGE,"E579")}),1.0]])]});
            var Q2;
            Q2=makeQuery(id+"F0.imprint","IMPRINT",FACE,{"disambiguationData":[TD([[makeQuery(id+"F0.imprint","IMPRINT",EDGE,{"derivedFrom":sQuery(id+"F0.wireOp",EDGE,"E489")}),1.0]])]});
            var Q3;
            Q3=makeQuery(id+"F0.imprint","IMPRINT",FACE,{"disambiguationData":[TD([[makeQuery(id+"F0.imprint","IMPRINT",EDGE,{"derivedFrom":sQuery(id+"F0.wireOp",EDGE,"E370")}),1.0]])]});
            var Q4;
            Q4=makeQuery(id+"F0.imprint","IMPRINT",FACE,{"disambiguationData":[TD([[makeQuery(id+"F0.imprint","IMPRINT",EDGE,{"derivedFrom":sQuery(id+"F0.wireOp",EDGE,"E436")}),1.0]])]});
            var Q5;
            Q5=makeQuery(id+"F0.imprint","IMPRINT",FACE,{"disambiguationData":[TD([[makeQuery(id+"F0.imprint","IMPRINT",EDGE,{"derivedFrom":sQuery(id+"F0.wireOp",EDGE,"E420")}),1.0]])]});
            var Q6;
            Q6=makeQuery(id+"F0.imprint","IMPRINT",FACE,{"disambiguationData":[TD([[makeQuery(id+"F0.imprint","IMPRINT",EDGE,{"derivedFrom":sQuery(id+"F0.wireOp",EDGE,"E414")}),1.0]])]});
            var Q7;
            Q7=makeQuery(id+"F0.imprint","IMPRINT",FACE,{"disambiguationData":[TD([[makeQuery(id+"F0.imprint","IMPRINT",EDGE,{"derivedFrom":sQuery(id+"F0.wireOp",EDGE,"E564")}),1.0]])]});
            var Q8;
            Q8=makeQuery(id+"F0.imprint","IMPRINT",FACE,{"disambiguationData":[TD([[makeQuery(id+"F0.imprint","IMPRINT",EDGE,{"derivedFrom":sQuery(id+"F0.wireOp",EDGE,"E609")}),1.0]])]});
            var Q9;
            Q9=makeQuery(id+"F0.imprint","IMPRINT",FACE,{"disambiguationData":[TD([[makeQuery(id+"F0.imprint","IMPRINT",EDGE,{"derivedFrom":sQuery(id+"F0.wireOp",EDGE,"E324")}),1.0]])]});
            var Q10;
            Q10=makeQuery(id+"F0.imprint","IMPRINT",FACE,{"disambiguationData":[TD([[makeQuery(id+"F0.imprint","IMPRINT",EDGE,{"derivedFrom":sQuery(id+"F0.wireOp",EDGE,"E343")}),1.0]])]});
            var Q11;
            Q11=makeQuery(id+"F0.imprint","IMPRINT",FACE,{"disambiguationData":[TD([[makeQuery(id+"F0.imprint","IMPRINT",EDGE,{"derivedFrom":sQuery(id+"F0.wireOp",EDGE,"E573")}),1.0]])]});
            var Q12;
            Q12=makeQuery(id+"F0.imprint","IMPRINT",FACE,{"disambiguationData":[TD([[makeQuery(id+"F0.imprint","IMPRINT",EDGE,{"derivedFrom":sQuery(id+"F0.wireOp",EDGE,"E586")}),1.0]])]});
            var Q13;
            Q13=makeQuery(id+"F0.imprint","IMPRINT",FACE,{"disambiguationData":[TD([[makeQuery(id+"F0.imprint","IMPRINT",EDGE,{"derivedFrom":sQuery(id+"F0.wireOp",EDGE,"E594")}),1.0]])]});
            var Q14;
            Q14=makeQuery(id+"F0.imprint","IMPRINT",FACE,{"disambiguationData":[TD([[makeQuery(id+"F0.imprint","IMPRINT",EDGE,{"derivedFrom":sQuery(id+"F0.wireOp",EDGE,"E601")}),1.0]])]});
            extrude(context, id + "F2", {"entities" : qUnion([Q0, Q1, Q2, Q3, Q4, Q5, Q6, Q7, Q8, Q9, Q10, Q11, Q12, Q13, Q14]), "operationType" : NewBodyOperationType.ADD, "depth" : 2.67 * mm});
        }
    });
